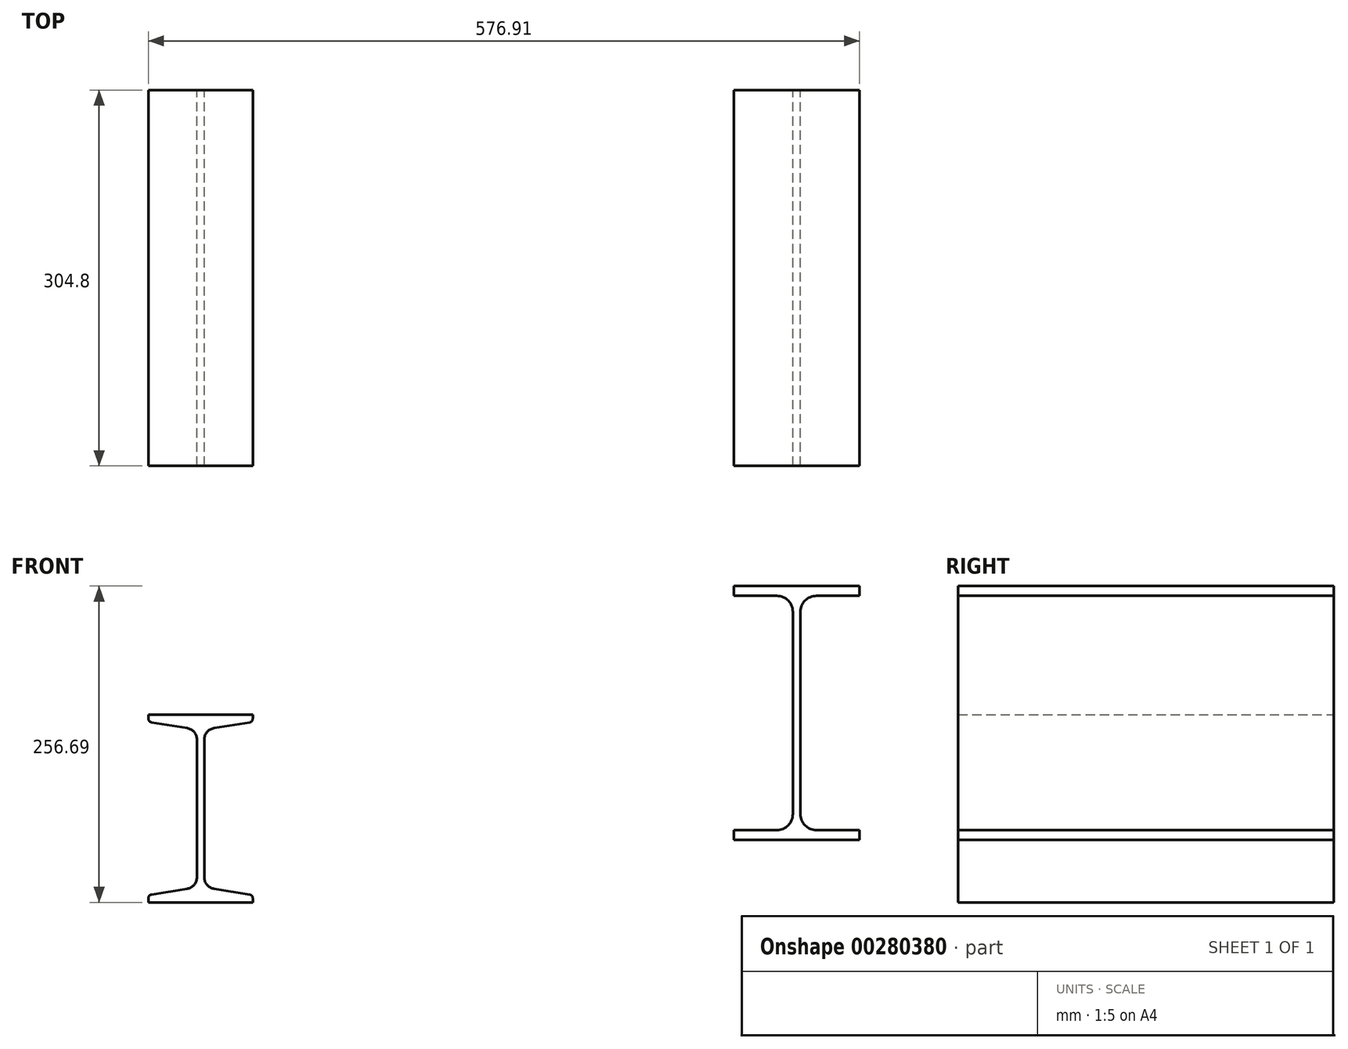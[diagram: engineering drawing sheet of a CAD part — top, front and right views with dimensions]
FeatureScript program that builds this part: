
annotation { "Feature Type Name" : "Feature", "Feature Type Description" : "" }
export const myFeature = defineFeature(function(context is Context, id is Id, definition is map)
    precondition{}
    {
        {
            var Q0;
            Q0=qCreatedBy(makeId("Front.planeOp"),FACE);
            var sketch = newSketch(context, id + "F0", { "sketchPlane" : qUnion([Q0])});
            skLineSegment(sketch, "E0", {"start": v(-460.28, 273.65) * mm, "end": v(-460.28, 271.12) * mm});
            skArc(sketch, "E1", {"start": v(-462.14, 268.95) * mm, "mid": v(-460.8, 269.7) * mm, "end": v(-460.28, 271.12) * mm});
            skLineSegment(sketch, "E2", {"start": v(-460.28, 197.45) * mm, "end": v(-460.28, 199.98) * mm});
            skArc(sketch, "E3", {"start": v(-460.28, 199.98) * mm, "mid": v(-460.8, 201.41) * mm, "end": v(-462.14, 202.16) * mm});
            skArc(sketch, "E4", {"start": v(-483.7, 265.5) * mm, "mid": v(-486.57, 263.88) * mm, "end": v(-487.71, 260.8) * mm});
            skLineSegment(sketch, "E5", {"start": v(-487.71, 210.31) * mm, "end": v(-487.71, 260.8) * mm});
            skLineSegment(sketch, "E6", {"start": v(-492.03, 210.31) * mm, "end": v(-492.03, 260.8) * mm});
            skArc(sketch, "E7", {"start": v(-492.03, 260.8) * mm, "mid": v(-493.17, 263.88) * mm, "end": v(-496.04, 265.5) * mm});
            skArc(sketch, "E8", {"start": v(-496.04, 205.61) * mm, "mid": v(-493.17, 207.22) * mm, "end": v(-492.03, 210.31) * mm});
            skArc(sketch, "E9", {"start": v(-487.71, 210.31) * mm, "mid": v(-486.57, 207.22) * mm, "end": v(-483.7, 205.61) * mm});
            skArc(sketch, "E10", {"start": v(-519.46, 271.12) * mm, "mid": v(-518.94, 269.7) * mm, "end": v(-517.6, 268.95) * mm});
            skLineSegment(sketch, "E11", {"start": v(-519.46, 273.65) * mm, "end": v(-519.46, 271.12) * mm});
            skLineSegment(sketch, "E12", {"start": v(-519.46, 197.45) * mm, "end": v(-519.46, 199.98) * mm});
            skArc(sketch, "E13", {"start": v(-517.6, 202.16) * mm, "mid": v(-518.94, 201.41) * mm, "end": v(-519.46, 199.98) * mm});
            skLineSegment(sketch, "E14", {"start": v(-517.6, 268.95) * mm, "end": v(-496.04, 265.5) * mm});
            skLineSegment(sketch, "E15", {"start": v(-517.6, 202.16) * mm, "end": v(-496.04, 205.61) * mm});
            skLineSegment(sketch, "E16", {"start": v(-462.14, 268.95) * mm, "end": v(-483.7, 265.5) * mm});
            skLineSegment(sketch, "E17", {"start": v(-462.14, 202.16) * mm, "end": v(-483.7, 205.61) * mm});
            skLineSegment(sketch, "E18", {"start": v(-519.46, 273.65) * mm, "end": v(-460.28, 273.65) * mm});
            skLineSegment(sketch, "E19", {"start": v(-519.46, 197.45) * mm, "end": v(-460.28, 197.45) * mm});
            skLineSegment(sketch, "E20", {"start": v(-495.3, 192.02) * mm, "end": v(-484.44, 202.89) * mm});
            skLineSegment(sketch, "E21", {"start": v(-495.3, 202.89) * mm, "end": v(-484.44, 192.02) * mm});
            skLineSegment(sketch, "E22", {"start": v(-351.6, 197.45) * mm, "end": v(-351.6, 222.85) * mm});
            skLineSegment(sketch, "E23", {"start": v(-410.78, 197.45) * mm, "end": v(-410.78, 222.85) * mm});
            skLineSegment(sketch, "E24", {"start": v(-383.35, 197.45) * mm, "end": v(-383.35, 222.85) * mm});
            skLineSegment(sketch, "E25", {"start": v(-379.03, 197.45) * mm, "end": v(-379.03, 222.85) * mm});
            skLineSegment(sketch, "E26", {"start": v(-351.6, 197.45) * mm, "end": v(-410.78, 197.45) * mm});
            skLineSegment(sketch, "E27", {"start": v(-351.6, 222.85) * mm, "end": v(-410.78, 222.85) * mm});
            skLineSegment(sketch, "E28", {"start": v(-386.63, 192.02) * mm, "end": v(-375.76, 202.89) * mm});
            skLineSegment(sketch, "E29", {"start": v(-386.63, 202.89) * mm, "end": v(-375.76, 192.02) * mm});
            skLineSegment(sketch, "E30", {"start": v(-259.79, 273.65) * mm, "end": v(-259.79, 197.45) * mm});
            skLineSegment(sketch, "E31", {"start": v(-285.19, 273.65) * mm, "end": v(-285.19, 197.45) * mm});
            skLineSegment(sketch, "E32", {"start": v(-259.79, 268.95) * mm, "end": v(-285.19, 268.95) * mm});
            skLineSegment(sketch, "E33", {"start": v(-259.79, 273.65) * mm, "end": v(-285.19, 273.65) * mm});
            skLineSegment(sketch, "E34", {"start": v(-259.79, 202.16) * mm, "end": v(-285.19, 202.16) * mm});
            skLineSegment(sketch, "E35", {"start": v(-259.79, 197.45) * mm, "end": v(-285.19, 197.45) * mm});
            skLineSegment(sketch, "E36", {"start": v(-290.62, 192.02) * mm, "end": v(-279.75, 202.89) * mm});
            skLineSegment(sketch, "E37", {"start": v(-290.62, 202.89) * mm, "end": v(-279.75, 192.02) * mm});
            skArc(sketch, "E38", {"start": v(-133.79, 268.95) * mm, "mid": v(-132.46, 269.7) * mm, "end": v(-131.93, 271.12) * mm});
            skLineSegment(sketch, "E39", {"start": v(-131.93, 273.65) * mm, "end": v(-131.93, 271.12) * mm});
            skLineSegment(sketch, "E40", {"start": v(-131.93, 197.45) * mm, "end": v(-131.93, 199.98) * mm});
            skArc(sketch, "E41", {"start": v(-131.93, 199.98) * mm, "mid": v(-132.46, 201.41) * mm, "end": v(-133.79, 202.16) * mm});
            skLineSegment(sketch, "E42", {"start": v(-193.8, 268.95) * mm, "end": v(-172.24, 265.5) * mm});
            skLineSegment(sketch, "E43", {"start": v(-195.66, 273.65) * mm, "end": v(-195.66, 271.12) * mm});
            skArc(sketch, "E44", {"start": v(-195.66, 271.12) * mm, "mid": v(-195.13, 269.7) * mm, "end": v(-193.8, 268.95) * mm});
            skArc(sketch, "E45", {"start": v(-159.36, 210.31) * mm, "mid": v(-158.23, 207.22) * mm, "end": v(-155.35, 205.61) * mm});
            skLineSegment(sketch, "E46", {"start": v(-193.8, 202.16) * mm, "end": v(-172.24, 205.61) * mm});
            skArc(sketch, "E47", {"start": v(-172.24, 205.61) * mm, "mid": v(-169.37, 207.22) * mm, "end": v(-168.23, 210.31) * mm});
            skLineSegment(sketch, "E48", {"start": v(-168.23, 210.31) * mm, "end": v(-168.23, 260.8) * mm});
            skLineSegment(sketch, "E49", {"start": v(-159.36, 210.31) * mm, "end": v(-159.36, 260.8) * mm});
            skLineSegment(sketch, "E50", {"start": v(-195.66, 197.45) * mm, "end": v(-195.66, 199.98) * mm});
            skArc(sketch, "E51", {"start": v(-193.8, 202.16) * mm, "mid": v(-195.13, 201.41) * mm, "end": v(-195.66, 199.98) * mm});
            skArc(sketch, "E52", {"start": v(-168.23, 260.8) * mm, "mid": v(-169.37, 263.88) * mm, "end": v(-172.24, 265.5) * mm});
            skArc(sketch, "E53", {"start": v(-155.35, 265.5) * mm, "mid": v(-158.23, 263.88) * mm, "end": v(-159.36, 260.8) * mm});
            skLineSegment(sketch, "E54", {"start": v(-133.79, 268.95) * mm, "end": v(-155.35, 265.5) * mm});
            skLineSegment(sketch, "E55", {"start": v(-133.79, 202.16) * mm, "end": v(-155.35, 205.61) * mm});
            skLineSegment(sketch, "E56", {"start": v(-195.66, 273.65) * mm, "end": v(-131.93, 273.65) * mm});
            skLineSegment(sketch, "E57", {"start": v(-195.66, 197.45) * mm, "end": v(-131.93, 197.45) * mm});
            skLineSegment(sketch, "E58", {"start": v(-169.23, 192.02) * mm, "end": v(-158.36, 202.89) * mm});
            skLineSegment(sketch, "E59", {"start": v(-169.23, 202.89) * mm, "end": v(-158.36, 192.02) * mm});
            skLineSegment(sketch, "E60", {"start": v(-23.24, 197.45) * mm, "end": v(-23.24, 222.85) * mm});
            skLineSegment(sketch, "E61", {"start": v(-59.54, 197.45) * mm, "end": v(-59.54, 222.85) * mm});
            skLineSegment(sketch, "E62", {"start": v(-50.67, 197.45) * mm, "end": v(-50.67, 222.85) * mm});
            skLineSegment(sketch, "E63", {"start": v(-86.97, 197.45) * mm, "end": v(-86.97, 222.85) * mm});
            skLineSegment(sketch, "E64", {"start": v(-23.24, 222.85) * mm, "end": v(-86.97, 222.85) * mm});
            skLineSegment(sketch, "E65", {"start": v(-23.24, 197.45) * mm, "end": v(-86.97, 197.45) * mm});
            skLineSegment(sketch, "E66", {"start": v(-60.54, 192.02) * mm, "end": v(-49.67, 202.89) * mm});
            skLineSegment(sketch, "E67", {"start": v(-60.54, 202.89) * mm, "end": v(-49.67, 192.02) * mm});
            skLineSegment(sketch, "E68", {"start": v(66.29, 273.65) * mm, "end": v(40.89, 273.65) * mm});
            skLineSegment(sketch, "E69", {"start": v(66.29, 268.95) * mm, "end": v(40.89, 268.95) * mm});
            skLineSegment(sketch, "E70", {"start": v(66.29, 202.16) * mm, "end": v(40.89, 202.16) * mm});
            skLineSegment(sketch, "E71", {"start": v(66.29, 197.45) * mm, "end": v(40.89, 197.45) * mm});
            skLineSegment(sketch, "E72", {"start": v(66.29, 273.65) * mm, "end": v(66.29, 197.45) * mm});
            skLineSegment(sketch, "E73", {"start": v(40.89, 273.65) * mm, "end": v(40.89, 197.45) * mm});
            skLineSegment(sketch, "E74", {"start": v(35.45, 192.02) * mm, "end": v(46.32, 202.89) * mm});
            skLineSegment(sketch, "E75", {"start": v(35.45, 202.89) * mm, "end": v(46.32, 192.02) * mm});
            skLineSegment(sketch, "E76", {"start": v(200.43, 299.05) * mm, "end": v(200.43, 296.42) * mm});
            skArc(sketch, "E77", {"start": v(198.5, 294.16) * mm, "mid": v(199.88, 294.94) * mm, "end": v(200.43, 296.42) * mm});
            skLineSegment(sketch, "E78", {"start": v(200.43, 197.45) * mm, "end": v(200.43, 200.09) * mm});
            skArc(sketch, "E79", {"start": v(200.43, 200.09) * mm, "mid": v(199.88, 201.57) * mm, "end": v(198.5, 202.35) * mm});
            skArc(sketch, "E80", {"start": v(170.08, 289.61) * mm, "mid": v(166.25, 287.46) * mm, "end": v(164.73, 283.34) * mm});
            skArc(sketch, "E81", {"start": v(159.83, 283.34) * mm, "mid": v(158.3, 287.46) * mm, "end": v(154.48, 289.61) * mm});
            skLineSegment(sketch, "E82", {"start": v(126.06, 294.16) * mm, "end": v(154.48, 289.61) * mm});
            skLineSegment(sketch, "E83", {"start": v(124.13, 299.05) * mm, "end": v(124.13, 296.42) * mm});
            skArc(sketch, "E84", {"start": v(124.13, 296.42) * mm, "mid": v(124.68, 294.94) * mm, "end": v(126.06, 294.16) * mm});
            skArc(sketch, "E85", {"start": v(164.73, 213.17) * mm, "mid": v(166.25, 209.05) * mm, "end": v(170.08, 206.9) * mm});
            skArc(sketch, "E86", {"start": v(154.48, 206.9) * mm, "mid": v(158.3, 209.05) * mm, "end": v(159.83, 213.17) * mm});
            skLineSegment(sketch, "E87", {"start": v(126.06, 202.35) * mm, "end": v(154.48, 206.9) * mm});
            skLineSegment(sketch, "E88", {"start": v(124.13, 197.45) * mm, "end": v(124.13, 200.09) * mm});
            skArc(sketch, "E89", {"start": v(126.06, 202.35) * mm, "mid": v(124.68, 201.57) * mm, "end": v(124.13, 200.09) * mm});
            skLineSegment(sketch, "E90", {"start": v(159.83, 213.17) * mm, "end": v(159.83, 283.34) * mm});
            skLineSegment(sketch, "E91", {"start": v(164.73, 213.17) * mm, "end": v(164.73, 283.34) * mm});
            skLineSegment(sketch, "E92", {"start": v(198.5, 294.16) * mm, "end": v(170.08, 289.61) * mm});
            skLineSegment(sketch, "E93", {"start": v(198.5, 202.35) * mm, "end": v(170.08, 206.9) * mm});
            skLineSegment(sketch, "E94", {"start": v(124.13, 299.05) * mm, "end": v(200.43, 299.05) * mm});
            skLineSegment(sketch, "E95", {"start": v(124.13, 197.45) * mm, "end": v(200.43, 197.45) * mm});
            skLineSegment(sketch, "E96", {"start": v(156.84, 192.02) * mm, "end": v(167.71, 202.89) * mm});
            skLineSegment(sketch, "E97", {"start": v(156.84, 202.89) * mm, "end": v(167.71, 192.02) * mm});
            skLineSegment(sketch, "E98", {"start": v(309.12, 197.45) * mm, "end": v(309.12, 222.85) * mm});
            skLineSegment(sketch, "E99", {"start": v(273.42, 197.45) * mm, "end": v(273.42, 222.33) * mm});
            skLineSegment(sketch, "E100", {"start": v(268.52, 197.45) * mm, "end": v(268.52, 222.85) * mm});
            skLineSegment(sketch, "E101", {"start": v(232.82, 197.45) * mm, "end": v(232.82, 222.85) * mm});
            skLineSegment(sketch, "E102", {"start": v(309.12, 222.85) * mm, "end": v(232.82, 222.85) * mm});
            skLineSegment(sketch, "E103", {"start": v(309.12, 197.45) * mm, "end": v(232.82, 197.45) * mm});
            skLineSegment(sketch, "E104", {"start": v(265.54, 192.02) * mm, "end": v(276.4, 202.89) * mm});
            skLineSegment(sketch, "E105", {"start": v(265.54, 202.89) * mm, "end": v(276.4, 192.02) * mm});
            skLineSegment(sketch, "E106", {"start": v(392.36, 299.05) * mm, "end": v(366.96, 299.05) * mm});
            skLineSegment(sketch, "E107", {"start": v(392.36, 294.16) * mm, "end": v(366.96, 294.16) * mm});
            skLineSegment(sketch, "E108", {"start": v(392.36, 202.35) * mm, "end": v(366.96, 202.35) * mm});
            skLineSegment(sketch, "E109", {"start": v(392.36, 197.45) * mm, "end": v(366.96, 197.45) * mm});
            skLineSegment(sketch, "E110", {"start": v(392.36, 299.05) * mm, "end": v(392.36, 197.45) * mm});
            skLineSegment(sketch, "E111", {"start": v(366.96, 299.05) * mm, "end": v(366.96, 197.45) * mm});
            skLineSegment(sketch, "E112", {"start": v(361.53, 192.02) * mm, "end": v(372.4, 202.89) * mm});
            skLineSegment(sketch, "E113", {"start": v(361.53, 202.89) * mm, "end": v(372.4, 192.02) * mm});
            skLineSegment(sketch, "E114", {"start": v(523.86, 299.05) * mm, "end": v(523.86, 296.22) * mm});
            skLineSegment(sketch, "E115", {"start": v(521.79, 293.79) * mm, "end": v(497.84, 289.96) * mm});
            skArc(sketch, "E116", {"start": v(521.79, 293.79) * mm, "mid": v(523.27, 294.62) * mm, "end": v(523.86, 296.22) * mm});
            skLineSegment(sketch, "E117", {"start": v(523.86, 197.45) * mm, "end": v(523.86, 200.28) * mm});
            skLineSegment(sketch, "E118", {"start": v(521.79, 202.72) * mm, "end": v(497.84, 206.55) * mm});
            skArc(sketch, "E119", {"start": v(523.86, 200.28) * mm, "mid": v(523.27, 201.88) * mm, "end": v(521.79, 202.72) * mm});
            skArc(sketch, "E120", {"start": v(484.21, 283.69) * mm, "mid": v(482.7, 287.8) * mm, "end": v(478.87, 289.96) * mm});
            skLineSegment(sketch, "E121", {"start": v(452.84, 299.05) * mm, "end": v(452.84, 296.22) * mm});
            skArc(sketch, "E122", {"start": v(452.84, 296.22) * mm, "mid": v(453.43, 294.62) * mm, "end": v(454.92, 293.79) * mm});
            skLineSegment(sketch, "E123", {"start": v(454.92, 293.79) * mm, "end": v(478.87, 289.96) * mm});
            skArc(sketch, "E124", {"start": v(478.87, 206.55) * mm, "mid": v(482.7, 208.7) * mm, "end": v(484.21, 212.82) * mm});
            skLineSegment(sketch, "E125", {"start": v(452.84, 197.45) * mm, "end": v(452.84, 200.28) * mm});
            skArc(sketch, "E126", {"start": v(454.92, 202.72) * mm, "mid": v(453.43, 201.88) * mm, "end": v(452.84, 200.28) * mm});
            skLineSegment(sketch, "E127", {"start": v(454.92, 202.72) * mm, "end": v(478.87, 206.55) * mm});
            skLineSegment(sketch, "E128", {"start": v(484.21, 212.82) * mm, "end": v(484.21, 283.69) * mm});
            skLineSegment(sketch, "E129", {"start": v(492.5, 212.82) * mm, "end": v(492.5, 283.69) * mm});
            skArc(sketch, "E130", {"start": v(497.84, 289.96) * mm, "mid": v(494.01, 287.8) * mm, "end": v(492.5, 283.69) * mm});
            skArc(sketch, "E131", {"start": v(492.5, 212.82) * mm, "mid": v(494.01, 208.7) * mm, "end": v(497.84, 206.55) * mm});
            skLineSegment(sketch, "E132", {"start": v(452.84, 299.05) * mm, "end": v(523.86, 299.05) * mm});
            skLineSegment(sketch, "E133", {"start": v(452.84, 197.45) * mm, "end": v(523.86, 197.45) * mm});
            skLineSegment(sketch, "E134", {"start": v(482.92, 192.02) * mm, "end": v(493.79, 202.89) * mm});
            skLineSegment(sketch, "E135", {"start": v(482.92, 202.89) * mm, "end": v(493.79, 192.02) * mm});
            skLineSegment(sketch, "E136", {"start": v(-454.36, -34.34) * mm, "end": v(-454.36, -8.94) * mm});
            skLineSegment(sketch, "E137", {"start": v(-494.01, -34.34) * mm, "end": v(-494.01, -8.94) * mm});
            skLineSegment(sketch, "E138", {"start": v(-485.73, -34.34) * mm, "end": v(-485.73, -8.94) * mm});
            skLineSegment(sketch, "E139", {"start": v(-525.38, -34.34) * mm, "end": v(-525.38, -8.94) * mm});
            skLineSegment(sketch, "E140", {"start": v(-454.36, -8.94) * mm, "end": v(-525.38, -8.94) * mm});
            skLineSegment(sketch, "E141", {"start": v(-454.36, -34.34) * mm, "end": v(-525.38, -34.34) * mm});
            skLineSegment(sketch, "E142", {"start": v(-495.3, -39.77) * mm, "end": v(-484.44, -28.9) * mm});
            skLineSegment(sketch, "E143", {"start": v(-495.3, -28.9) * mm, "end": v(-484.44, -39.77) * mm});
            skLineSegment(sketch, "E144", {"start": v(-368.48, 67.26) * mm, "end": v(-368.48, -34.34) * mm});
            skLineSegment(sketch, "E145", {"start": v(-393.88, 67.26) * mm, "end": v(-393.88, -34.34) * mm});
            skLineSegment(sketch, "E146", {"start": v(-368.48, 67.26) * mm, "end": v(-393.88, 67.26) * mm});
            skLineSegment(sketch, "E147", {"start": v(-368.48, 62) * mm, "end": v(-393.88, 62) * mm});
            skLineSegment(sketch, "E148", {"start": v(-368.48, -29.07) * mm, "end": v(-393.88, -29.07) * mm});
            skLineSegment(sketch, "E149", {"start": v(-368.48, -34.34) * mm, "end": v(-393.88, -34.34) * mm});
            skLineSegment(sketch, "E150", {"start": v(-399.31, -39.77) * mm, "end": v(-388.45, -28.9) * mm});
            skLineSegment(sketch, "E151", {"start": v(-399.31, -28.9) * mm, "end": v(-388.45, -39.77) * mm});
            skArc(sketch, "E152", {"start": v(-236.98, 85.96) * mm, "mid": v(-235.09, 87.02) * mm, "end": v(-234.34, 89.06) * mm});
            skLineSegment(sketch, "E153", {"start": v(-234.34, 92.66) * mm, "end": v(-234.34, 89.06) * mm});
            skArc(sketch, "E154", {"start": v(-275.2, 73.94) * mm, "mid": v(-277.1, 79.1) * mm, "end": v(-281.89, 81.78) * mm});
            skArc(sketch, "E155", {"start": v(-263.09, 81.78) * mm, "mid": v(-267.87, 79.1) * mm, "end": v(-269.77, 73.94) * mm});
            skLineSegment(sketch, "E156", {"start": v(-236.98, 85.96) * mm, "end": v(-263.09, 81.78) * mm});
            skArc(sketch, "E157", {"start": v(-234.34, -30.73) * mm, "mid": v(-235.09, -28.7) * mm, "end": v(-236.98, -27.63) * mm});
            skLineSegment(sketch, "E158", {"start": v(-234.34, -34.34) * mm, "end": v(-234.34, -30.73) * mm});
            skArc(sketch, "E159", {"start": v(-269.77, -15.62) * mm, "mid": v(-267.87, -20.77) * mm, "end": v(-263.09, -23.45) * mm});
            skArc(sketch, "E160", {"start": v(-281.89, -23.45) * mm, "mid": v(-277.1, -20.77) * mm, "end": v(-275.2, -15.62) * mm});
            skLineSegment(sketch, "E161", {"start": v(-236.98, -27.63) * mm, "end": v(-263.09, -23.45) * mm});
            skLineSegment(sketch, "E162", {"start": v(-275.2, -15.62) * mm, "end": v(-275.2, 73.94) * mm});
            skLineSegment(sketch, "E163", {"start": v(-269.77, -15.62) * mm, "end": v(-269.77, 73.94) * mm});
            skLineSegment(sketch, "E164", {"start": v(-310.64, 92.66) * mm, "end": v(-310.64, 89.06) * mm});
            skArc(sketch, "E165", {"start": v(-310.64, 89.06) * mm, "mid": v(-309.89, 87.02) * mm, "end": v(-308, 85.96) * mm});
            skArc(sketch, "E166", {"start": v(-308, -27.63) * mm, "mid": v(-309.89, -28.7) * mm, "end": v(-310.64, -30.73) * mm});
            skLineSegment(sketch, "E167", {"start": v(-310.64, -34.34) * mm, "end": v(-310.64, -30.73) * mm});
            skLineSegment(sketch, "E168", {"start": v(-308, 85.96) * mm, "end": v(-281.89, 81.78) * mm});
            skLineSegment(sketch, "E169", {"start": v(-308, -27.63) * mm, "end": v(-281.89, -23.45) * mm});
            skLineSegment(sketch, "E170", {"start": v(-310.64, 92.66) * mm, "end": v(-234.34, 92.66) * mm});
            skLineSegment(sketch, "E171", {"start": v(-310.64, -34.34) * mm, "end": v(-234.34, -34.34) * mm});
            skLineSegment(sketch, "E172", {"start": v(-277.92, -39.77) * mm, "end": v(-267.05, -28.9) * mm});
            skLineSegment(sketch, "E173", {"start": v(-277.92, -28.9) * mm, "end": v(-267.05, -39.77) * mm});
            skLineSegment(sketch, "E174", {"start": v(-125.65, -34.34) * mm, "end": v(-125.65, -8.94) * mm});
            skLineSegment(sketch, "E175", {"start": v(-166.51, -34.34) * mm, "end": v(-166.51, -8.94) * mm});
            skLineSegment(sketch, "E176", {"start": v(-161.08, -34.34) * mm, "end": v(-161.08, -8.94) * mm});
            skLineSegment(sketch, "E177", {"start": v(-201.95, -34.34) * mm, "end": v(-201.95, -8.94) * mm});
            skLineSegment(sketch, "E178", {"start": v(-201.95, -8.94) * mm, "end": v(-125.65, -8.94) * mm});
            skLineSegment(sketch, "E179", {"start": v(-201.95, -34.34) * mm, "end": v(-125.65, -34.34) * mm});
            skLineSegment(sketch, "E180", {"start": v(-169.23, -39.77) * mm, "end": v(-158.36, -28.9) * mm});
            skLineSegment(sketch, "E181", {"start": v(-169.23, -28.9) * mm, "end": v(-158.36, -39.77) * mm});
            skLineSegment(sketch, "E182", {"start": v(-42.4, 92.66) * mm, "end": v(-67.8, 92.66) * mm});
            skLineSegment(sketch, "E183", {"start": v(-42.4, 85.96) * mm, "end": v(-67.8, 85.96) * mm});
            skLineSegment(sketch, "E184", {"start": v(-42.4, -27.63) * mm, "end": v(-67.8, -27.63) * mm});
            skLineSegment(sketch, "E185", {"start": v(-42.4, -34.34) * mm, "end": v(-67.8, -34.34) * mm});
            skLineSegment(sketch, "E186", {"start": v(-42.4, 92.66) * mm, "end": v(-42.4, -34.34) * mm});
            skLineSegment(sketch, "E187", {"start": v(-67.8, 92.66) * mm, "end": v(-67.8, -34.34) * mm});
            skLineSegment(sketch, "E188", {"start": v(-73.24, -39.77) * mm, "end": v(-62.37, -28.9) * mm});
            skLineSegment(sketch, "E189", {"start": v(-73.24, -28.9) * mm, "end": v(-62.37, -39.77) * mm});
            skLineSegment(sketch, "E190", {"start": v(95.3, 92.66) * mm, "end": v(95.3, 89.54) * mm});
            skArc(sketch, "E191", {"start": v(93, 86.85) * mm, "mid": v(94.64, 87.77) * mm, "end": v(95.3, 89.54) * mm});
            skArc(sketch, "E192", {"start": v(66.54, 82.62) * mm, "mid": v(61.76, 79.93) * mm, "end": v(59.86, 74.78) * mm});
            skArc(sketch, "E193", {"start": v(47.31, 74.78) * mm, "mid": v(45.42, 79.93) * mm, "end": v(40.63, 82.62) * mm});
            skLineSegment(sketch, "E194", {"start": v(93, 86.85) * mm, "end": v(66.54, 82.62) * mm});
            skLineSegment(sketch, "E195", {"start": v(95.3, -34.34) * mm, "end": v(95.3, -31.21) * mm});
            skArc(sketch, "E196", {"start": v(95.3, -31.21) * mm, "mid": v(94.64, -29.45) * mm, "end": v(93, -28.52) * mm});
            skArc(sketch, "E197", {"start": v(40.63, -24.3) * mm, "mid": v(45.42, -21.6) * mm, "end": v(47.31, -16.45) * mm});
            skArc(sketch, "E198", {"start": v(59.86, -16.45) * mm, "mid": v(61.76, -21.6) * mm, "end": v(66.54, -24.3) * mm});
            skLineSegment(sketch, "E199", {"start": v(93, -28.52) * mm, "end": v(66.54, -24.3) * mm});
            skLineSegment(sketch, "E200", {"start": v(47.31, -16.45) * mm, "end": v(47.31, 74.78) * mm});
            skLineSegment(sketch, "E201", {"start": v(59.86, -16.45) * mm, "end": v(59.86, 74.78) * mm});
            skLineSegment(sketch, "E202", {"start": v(11.88, 92.66) * mm, "end": v(11.88, 89.54) * mm});
            skArc(sketch, "E203", {"start": v(11.88, 89.54) * mm, "mid": v(12.53, 87.77) * mm, "end": v(14.17, 86.85) * mm});
            skLineSegment(sketch, "E204", {"start": v(11.88, -34.34) * mm, "end": v(11.88, -31.21) * mm});
            skArc(sketch, "E205", {"start": v(14.17, -28.52) * mm, "mid": v(12.53, -29.45) * mm, "end": v(11.88, -31.21) * mm});
            skLineSegment(sketch, "E206", {"start": v(14.17, 86.85) * mm, "end": v(40.63, 82.62) * mm});
            skLineSegment(sketch, "E207", {"start": v(14.17, -28.52) * mm, "end": v(40.63, -24.3) * mm});
            skLineSegment(sketch, "E208", {"start": v(11.88, 92.66) * mm, "end": v(95.3, 92.66) * mm});
            skLineSegment(sketch, "E209", {"start": v(11.88, -34.34) * mm, "end": v(95.3, -34.34) * mm});
            skLineSegment(sketch, "E210", {"start": v(48.15, -39.77) * mm, "end": v(59.02, -28.9) * mm});
            skLineSegment(sketch, "E211", {"start": v(48.15, -28.9) * mm, "end": v(59.02, -39.77) * mm});
            skLineSegment(sketch, "E212", {"start": v(203.99, -34.34) * mm, "end": v(203.99, -8.94) * mm});
            skLineSegment(sketch, "E213", {"start": v(156, -34.34) * mm, "end": v(156, -8.94) * mm});
            skLineSegment(sketch, "E214", {"start": v(168.55, -34.34) * mm, "end": v(168.55, -8.94) * mm});
            skLineSegment(sketch, "E215", {"start": v(120.57, -34.34) * mm, "end": v(120.57, -8.94) * mm});
            skLineSegment(sketch, "E216", {"start": v(203.99, -8.94) * mm, "end": v(120.57, -8.94) * mm});
            skLineSegment(sketch, "E217", {"start": v(203.99, -34.34) * mm, "end": v(120.57, -34.34) * mm});
            skLineSegment(sketch, "E218", {"start": v(156.84, -39.77) * mm, "end": v(167.71, -28.9) * mm});
            skLineSegment(sketch, "E219", {"start": v(156.84, -28.9) * mm, "end": v(167.71, -39.77) * mm});
            skLineSegment(sketch, "E220", {"start": v(283.67, 92.66) * mm, "end": v(258.27, 92.66) * mm});
            skLineSegment(sketch, "E221", {"start": v(283.67, 86.85) * mm, "end": v(258.27, 86.85) * mm});
            skLineSegment(sketch, "E222", {"start": v(283.67, -28.52) * mm, "end": v(258.27, -28.52) * mm});
            skLineSegment(sketch, "E223", {"start": v(283.67, -34.34) * mm, "end": v(258.27, -34.34) * mm});
            skLineSegment(sketch, "E224", {"start": v(283.67, 92.66) * mm, "end": v(283.67, -34.34) * mm});
            skLineSegment(sketch, "E225", {"start": v(258.27, 92.66) * mm, "end": v(258.27, -34.34) * mm});
            skLineSegment(sketch, "E226", {"start": v(252.84, -39.77) * mm, "end": v(263.7, -28.9) * mm});
            skLineSegment(sketch, "E227", {"start": v(252.84, -28.9) * mm, "end": v(263.7, -39.77) * mm});
            skArc(sketch, "E228", {"start": v(419.47, 111.7) * mm, "mid": v(421.26, 112.7) * mm, "end": v(421.98, 114.64) * mm});
            skArc(sketch, "E229", {"start": v(390.63, 107.08) * mm, "mid": v(384.89, 103.85) * mm, "end": v(382.6, 97.67) * mm});
            skArc(sketch, "E230", {"start": v(376.72, 97.67) * mm, "mid": v(374.44, 103.85) * mm, "end": v(368.7, 107.08) * mm});
            skLineSegment(sketch, "E231", {"start": v(419.47, 111.7) * mm, "end": v(390.63, 107.08) * mm});
            skLineSegment(sketch, "E232", {"start": v(421.98, 118.06) * mm, "end": v(421.98, 114.64) * mm});
            skLineSegment(sketch, "E233", {"start": v(421.98, -34.34) * mm, "end": v(421.98, -30.91) * mm});
            skArc(sketch, "E234", {"start": v(421.98, -30.91) * mm, "mid": v(421.26, -28.98) * mm, "end": v(419.47, -27.97) * mm});
            skArc(sketch, "E235", {"start": v(382.6, -13.95) * mm, "mid": v(384.89, -20.13) * mm, "end": v(390.63, -23.35) * mm});
            skArc(sketch, "E236", {"start": v(368.7, -23.35) * mm, "mid": v(374.44, -20.13) * mm, "end": v(376.72, -13.95) * mm});
            skLineSegment(sketch, "E237", {"start": v(419.47, -27.97) * mm, "end": v(390.63, -23.35) * mm});
            skLineSegment(sketch, "E238", {"start": v(376.72, -13.95) * mm, "end": v(376.72, 97.67) * mm});
            skLineSegment(sketch, "E239", {"start": v(382.6, -13.95) * mm, "end": v(382.6, 97.67) * mm});
            skArc(sketch, "E240", {"start": v(337.35, 114.64) * mm, "mid": v(338.06, 112.7) * mm, "end": v(339.86, 111.7) * mm});
            skLineSegment(sketch, "E241", {"start": v(337.35, 118.06) * mm, "end": v(337.35, 114.64) * mm});
            skLineSegment(sketch, "E242", {"start": v(337.35, -34.34) * mm, "end": v(337.35, -30.91) * mm});
            skArc(sketch, "E243", {"start": v(339.86, -27.97) * mm, "mid": v(338.06, -28.98) * mm, "end": v(337.35, -30.91) * mm});
            skLineSegment(sketch, "E244", {"start": v(339.86, 111.7) * mm, "end": v(368.7, 107.08) * mm});
            skLineSegment(sketch, "E245", {"start": v(339.86, -27.97) * mm, "end": v(368.7, -23.35) * mm});
            skLineSegment(sketch, "E246", {"start": v(337.35, 118.06) * mm, "end": v(421.98, 118.06) * mm});
            skLineSegment(sketch, "E247", {"start": v(337.35, -34.34) * mm, "end": v(421.98, -34.34) * mm});
            skLineSegment(sketch, "E248", {"start": v(374.23, -39.77) * mm, "end": v(385.1, -28.9) * mm});
            skLineSegment(sketch, "E249", {"start": v(374.23, -28.9) * mm, "end": v(385.1, -39.77) * mm});
            skLineSegment(sketch, "E250", {"start": v(530.66, -34.34) * mm, "end": v(530.66, -8.94) * mm});
            skLineSegment(sketch, "E251", {"start": v(491.29, -34.34) * mm, "end": v(491.29, -8.94) * mm});
            skLineSegment(sketch, "E252", {"start": v(485.4, -34.34) * mm, "end": v(485.4, -8.94) * mm});
            skLineSegment(sketch, "E253", {"start": v(446.02, -34.34) * mm, "end": v(446.02, -8.94) * mm});
            skLineSegment(sketch, "E254", {"start": v(530.66, -8.94) * mm, "end": v(446.02, -8.94) * mm});
            skLineSegment(sketch, "E255", {"start": v(530.66, -34.34) * mm, "end": v(446.02, -34.34) * mm});
            skLineSegment(sketch, "E256", {"start": v(482.9, -39.77) * mm, "end": v(493.78, -28.9) * mm});
            skLineSegment(sketch, "E257", {"start": v(482.9, -28.9) * mm, "end": v(493.78, -39.77) * mm});
            skLineSegment(sketch, "E258", {"start": v(-477.17, -113.73) * mm, "end": v(-502.57, -113.73) * mm});
            skLineSegment(sketch, "E259", {"start": v(-477.17, -120.1) * mm, "end": v(-502.57, -120.1) * mm});
            skLineSegment(sketch, "E260", {"start": v(-477.17, -259.76) * mm, "end": v(-502.57, -259.76) * mm});
            skLineSegment(sketch, "E261", {"start": v(-477.17, -266.13) * mm, "end": v(-502.57, -266.13) * mm});
            skLineSegment(sketch, "E262", {"start": v(-477.17, -113.73) * mm, "end": v(-477.17, -266.13) * mm});
            skLineSegment(sketch, "E263", {"start": v(-502.57, -113.73) * mm, "end": v(-502.57, -266.13) * mm});
            skLineSegment(sketch, "E264", {"start": v(-508, -271.56) * mm, "end": v(-497.14, -260.7) * mm});
            skLineSegment(sketch, "E265", {"start": v(-508, -260.7) * mm, "end": v(-497.14, -271.56) * mm});
            skLineSegment(sketch, "E266", {"start": v(-335.9, -113.73) * mm, "end": v(-335.9, -117.15) * mm});
            skArc(sketch, "E267", {"start": v(-338.42, -120.1) * mm, "mid": v(-336.62, -119.09) * mm, "end": v(-335.9, -117.15) * mm});
            skArc(sketch, "E268", {"start": v(-367.25, -124.71) * mm, "mid": v(-373, -127.94) * mm, "end": v(-375.27, -134.12) * mm});
            skLineSegment(sketch, "E269", {"start": v(-338.42, -120.1) * mm, "end": v(-367.25, -124.71) * mm});
            skLineSegment(sketch, "E270", {"start": v(-375.27, -245.74) * mm, "end": v(-375.27, -134.12) * mm});
            skLineSegment(sketch, "E271", {"start": v(-426.46, -113.73) * mm, "end": v(-426.46, -117.15) * mm});
            skArc(sketch, "E272", {"start": v(-387.09, -134.12) * mm, "mid": v(-389.36, -127.94) * mm, "end": v(-395.1, -124.71) * mm});
            skLineSegment(sketch, "E273", {"start": v(-423.94, -120.1) * mm, "end": v(-395.1, -124.71) * mm});
            skArc(sketch, "E274", {"start": v(-426.46, -117.15) * mm, "mid": v(-425.74, -119.09) * mm, "end": v(-423.94, -120.1) * mm});
            skLineSegment(sketch, "E275", {"start": v(-387.09, -245.74) * mm, "end": v(-387.09, -134.12) * mm});
            skLineSegment(sketch, "E276", {"start": v(-426.46, -113.73) * mm, "end": v(-335.9, -113.73) * mm});
            skLineSegment(sketch, "E277", {"start": v(-335.9, -266.13) * mm, "end": v(-335.9, -262.7) * mm});
            skArc(sketch, "E278", {"start": v(-335.9, -262.7) * mm, "mid": v(-336.62, -260.77) * mm, "end": v(-338.42, -259.76) * mm});
            skLineSegment(sketch, "E279", {"start": v(-338.42, -259.76) * mm, "end": v(-367.25, -255.14) * mm});
            skLineSegment(sketch, "E280", {"start": v(-426.46, -266.13) * mm, "end": v(-426.46, -262.7) * mm});
            skLineSegment(sketch, "E281", {"start": v(-423.94, -259.76) * mm, "end": v(-395.1, -255.14) * mm});
            skArc(sketch, "E282", {"start": v(-423.94, -259.76) * mm, "mid": v(-425.74, -260.77) * mm, "end": v(-426.46, -262.7) * mm});
            skLineSegment(sketch, "E283", {"start": v(-426.46, -266.13) * mm, "end": v(-335.9, -266.13) * mm});
            skArc(sketch, "E284", {"start": v(-395.1, -255.14) * mm, "mid": v(-389.36, -251.92) * mm, "end": v(-387.09, -245.74) * mm});
            skArc(sketch, "E285", {"start": v(-375.27, -245.74) * mm, "mid": v(-373, -251.92) * mm, "end": v(-367.25, -255.14) * mm});
            skLineSegment(sketch, "E286", {"start": v(-386.61, -271.56) * mm, "end": v(-375.75, -260.7) * mm});
            skLineSegment(sketch, "E287", {"start": v(-386.61, -260.7) * mm, "end": v(-375.75, -271.56) * mm});
            skLineSegment(sketch, "E288", {"start": v(-227.21, -240.73) * mm, "end": v(-317.76, -240.73) * mm});
            skLineSegment(sketch, "E289", {"start": v(-227.21, -266.13) * mm, "end": v(-317.76, -266.13) * mm});
            skLineSegment(sketch, "E290", {"start": v(-227.21, -266.13) * mm, "end": v(-227.21, -240.73) * mm});
            skLineSegment(sketch, "E291", {"start": v(-317.76, -266.13) * mm, "end": v(-317.76, -240.73) * mm});
            skLineSegment(sketch, "E292", {"start": v(-278.4, -266.13) * mm, "end": v(-278.4, -240.73) * mm});
            skLineSegment(sketch, "E293", {"start": v(-266.58, -266.13) * mm, "end": v(-266.58, -240.73) * mm});
            skLineSegment(sketch, "E294", {"start": v(-277.92, -271.56) * mm, "end": v(-267.05, -260.7) * mm});
            skLineSegment(sketch, "E295", {"start": v(-277.92, -260.7) * mm, "end": v(-267.05, -271.56) * mm});
            skLineSegment(sketch, "E296", {"start": v(-151.1, -113.73) * mm, "end": v(-176.5, -113.73) * mm});
            skLineSegment(sketch, "E297", {"start": v(-151.1, -120.1) * mm, "end": v(-176.5, -120.1) * mm});
            skLineSegment(sketch, "E298", {"start": v(-151.1, -259.76) * mm, "end": v(-176.5, -259.76) * mm});
            skLineSegment(sketch, "E299", {"start": v(-151.1, -266.13) * mm, "end": v(-176.5, -266.13) * mm});
            skLineSegment(sketch, "E300", {"start": v(-151.1, -113.73) * mm, "end": v(-151.1, -266.13) * mm});
            skLineSegment(sketch, "E301", {"start": v(-176.5, -113.73) * mm, "end": v(-176.5, -266.13) * mm});
            skLineSegment(sketch, "E302", {"start": v(-181.93, -271.56) * mm, "end": v(-171.06, -260.7) * mm});
            skLineSegment(sketch, "E303", {"start": v(-181.93, -260.7) * mm, "end": v(-171.06, -271.56) * mm});
            skSolve(sketch);
        }
        {
            var Q0;
            Q0 = qSketchRegion(id + "F0", true);
            extrude(context, id + "F1", {"entities" : qUnion([Q0]), "depth" : 304.8 * mm});
        }
        {
            var Q0;
            Q0=makeQuery(id+"F1.opExtrude","SWEPT_BODY",BODY,{"disambiguationData":[OSD([sQuery(id+"F0.wireOp",EDGE,"E144"),sQuery(id+"F0.wireOp",EDGE,"E145"),sQuery(id+"F0.wireOp",EDGE,"E146"),sQuery(id+"F0.wireOp",EDGE,"E149")])]});
            var Q1;
            Q1=makeQuery(id+"F1.opExtrude","SWEPT_BODY",BODY,{"disambiguationData":[OSD([sQuery(id+"F0.wireOp",EDGE,"E0"),sQuery(id+"F0.wireOp",EDGE,"E1"),sQuery(id+"F0.wireOp",EDGE,"E2"),sQuery(id+"F0.wireOp",EDGE,"E3"),sQuery(id+"F0.wireOp",EDGE,"E4"),sQuery(id+"F0.wireOp",EDGE,"E5"),sQuery(id+"F0.wireOp",EDGE,"E6"),sQuery(id+"F0.wireOp",EDGE,"E7"),sQuery(id+"F0.wireOp",EDGE,"E8"),sQuery(id+"F0.wireOp",EDGE,"E9"),sQuery(id+"F0.wireOp",EDGE,"E10"),sQuery(id+"F0.wireOp",EDGE,"E11"),sQuery(id+"F0.wireOp",EDGE,"E12"),sQuery(id+"F0.wireOp",EDGE,"E13"),sQuery(id+"F0.wireOp",EDGE,"E14"),sQuery(id+"F0.wireOp",EDGE,"E15"),sQuery(id+"F0.wireOp",EDGE,"E16"),sQuery(id+"F0.wireOp",EDGE,"E17"),sQuery(id+"F0.wireOp",EDGE,"E18"),sQuery(id+"F0.wireOp",EDGE,"E19")])]});
            var Q2;
            Q2=makeQuery(id+"F1.opExtrude","SWEPT_BODY",BODY,{"disambiguationData":[OSD([sQuery(id+"F0.wireOp",EDGE,"E22"),sQuery(id+"F0.wireOp",EDGE,"E23"),sQuery(id+"F0.wireOp",EDGE,"E26"),sQuery(id+"F0.wireOp",EDGE,"E27")])]});
            var Q3;
            Q3=makeQuery(id+"F1.opExtrude","SWEPT_BODY",BODY,{"disambiguationData":[OSD([sQuery(id+"F0.wireOp",EDGE,"E30"),sQuery(id+"F0.wireOp",EDGE,"E31"),sQuery(id+"F0.wireOp",EDGE,"E33"),sQuery(id+"F0.wireOp",EDGE,"E35")])]});
            var Q4;
            Q4=makeQuery(id+"F1.opExtrude","SWEPT_BODY",BODY,{"disambiguationData":[OSD([sQuery(id+"F0.wireOp",EDGE,"E38"),sQuery(id+"F0.wireOp",EDGE,"E39"),sQuery(id+"F0.wireOp",EDGE,"E40"),sQuery(id+"F0.wireOp",EDGE,"E41"),sQuery(id+"F0.wireOp",EDGE,"E42"),sQuery(id+"F0.wireOp",EDGE,"E43"),sQuery(id+"F0.wireOp",EDGE,"E44"),sQuery(id+"F0.wireOp",EDGE,"E45"),sQuery(id+"F0.wireOp",EDGE,"E46"),sQuery(id+"F0.wireOp",EDGE,"E47"),sQuery(id+"F0.wireOp",EDGE,"E48"),sQuery(id+"F0.wireOp",EDGE,"E49"),sQuery(id+"F0.wireOp",EDGE,"E50"),sQuery(id+"F0.wireOp",EDGE,"E51"),sQuery(id+"F0.wireOp",EDGE,"E52"),sQuery(id+"F0.wireOp",EDGE,"E53"),sQuery(id+"F0.wireOp",EDGE,"E54"),sQuery(id+"F0.wireOp",EDGE,"E55"),sQuery(id+"F0.wireOp",EDGE,"E56"),sQuery(id+"F0.wireOp",EDGE,"E57")])]});
            var Q5;
            Q5=makeQuery(id+"F1.opExtrude","SWEPT_BODY",BODY,{"disambiguationData":[OSD([sQuery(id+"F0.wireOp",EDGE,"E60"),sQuery(id+"F0.wireOp",EDGE,"E63"),sQuery(id+"F0.wireOp",EDGE,"E64"),sQuery(id+"F0.wireOp",EDGE,"E65")])]});
            var Q6;
            Q6=makeQuery(id+"F1.opExtrude","SWEPT_BODY",BODY,{"disambiguationData":[OSD([sQuery(id+"F0.wireOp",EDGE,"E68"),sQuery(id+"F0.wireOp",EDGE,"E71"),sQuery(id+"F0.wireOp",EDGE,"E72"),sQuery(id+"F0.wireOp",EDGE,"E73")])]});
            var Q7;
            Q7=makeQuery(id+"F1.opExtrude","SWEPT_BODY",BODY,{"disambiguationData":[OSD([sQuery(id+"F0.wireOp",EDGE,"E76"),sQuery(id+"F0.wireOp",EDGE,"E77"),sQuery(id+"F0.wireOp",EDGE,"E78"),sQuery(id+"F0.wireOp",EDGE,"E79"),sQuery(id+"F0.wireOp",EDGE,"E80"),sQuery(id+"F0.wireOp",EDGE,"E81"),sQuery(id+"F0.wireOp",EDGE,"E82"),sQuery(id+"F0.wireOp",EDGE,"E83"),sQuery(id+"F0.wireOp",EDGE,"E84"),sQuery(id+"F0.wireOp",EDGE,"E85"),sQuery(id+"F0.wireOp",EDGE,"E86"),sQuery(id+"F0.wireOp",EDGE,"E87"),sQuery(id+"F0.wireOp",EDGE,"E88"),sQuery(id+"F0.wireOp",EDGE,"E89"),sQuery(id+"F0.wireOp",EDGE,"E90"),sQuery(id+"F0.wireOp",EDGE,"E91"),sQuery(id+"F0.wireOp",EDGE,"E92"),sQuery(id+"F0.wireOp",EDGE,"E93"),sQuery(id+"F0.wireOp",EDGE,"E94"),sQuery(id+"F0.wireOp",EDGE,"E95")])]});
            var Q8;
            Q8=makeQuery(id+"F1.opExtrude","SWEPT_BODY",BODY,{"disambiguationData":[OSD([sQuery(id+"F0.wireOp",EDGE,"E98"),sQuery(id+"F0.wireOp",EDGE,"E101"),sQuery(id+"F0.wireOp",EDGE,"E102"),sQuery(id+"F0.wireOp",EDGE,"E103")])]});
            var Q9;
            Q9=makeQuery(id+"F1.opExtrude","SWEPT_BODY",BODY,{"disambiguationData":[OSD([sQuery(id+"F0.wireOp",EDGE,"E106"),sQuery(id+"F0.wireOp",EDGE,"E109"),sQuery(id+"F0.wireOp",EDGE,"E110"),sQuery(id+"F0.wireOp",EDGE,"E111")])]});
            var Q10;
            Q10=makeQuery(id+"F1.opExtrude","SWEPT_BODY",BODY,{"disambiguationData":[OSD([sQuery(id+"F0.wireOp",EDGE,"E114"),sQuery(id+"F0.wireOp",EDGE,"E115"),sQuery(id+"F0.wireOp",EDGE,"E116"),sQuery(id+"F0.wireOp",EDGE,"E117"),sQuery(id+"F0.wireOp",EDGE,"E118"),sQuery(id+"F0.wireOp",EDGE,"E119"),sQuery(id+"F0.wireOp",EDGE,"E120"),sQuery(id+"F0.wireOp",EDGE,"E121"),sQuery(id+"F0.wireOp",EDGE,"E122"),sQuery(id+"F0.wireOp",EDGE,"E123"),sQuery(id+"F0.wireOp",EDGE,"E124"),sQuery(id+"F0.wireOp",EDGE,"E125"),sQuery(id+"F0.wireOp",EDGE,"E126"),sQuery(id+"F0.wireOp",EDGE,"E127"),sQuery(id+"F0.wireOp",EDGE,"E128"),sQuery(id+"F0.wireOp",EDGE,"E129"),sQuery(id+"F0.wireOp",EDGE,"E130"),sQuery(id+"F0.wireOp",EDGE,"E131"),sQuery(id+"F0.wireOp",EDGE,"E132"),sQuery(id+"F0.wireOp",EDGE,"E133")])]});
            var Q11;
            Q11=makeQuery(id+"F1.opExtrude","SWEPT_BODY",BODY,{"disambiguationData":[OSD([sQuery(id+"F0.wireOp",EDGE,"E136"),sQuery(id+"F0.wireOp",EDGE,"E139"),sQuery(id+"F0.wireOp",EDGE,"E140"),sQuery(id+"F0.wireOp",EDGE,"E141")])]});
            var Q12;
            Q12=makeQuery(id+"F1.opExtrude","SWEPT_BODY",BODY,{"disambiguationData":[OSD([sQuery(id+"F0.wireOp",EDGE,"E174"),sQuery(id+"F0.wireOp",EDGE,"E177"),sQuery(id+"F0.wireOp",EDGE,"E178"),sQuery(id+"F0.wireOp",EDGE,"E179")])]});
            var Q13;
            Q13=makeQuery(id+"F1.opExtrude","SWEPT_BODY",BODY,{"disambiguationData":[OSD([sQuery(id+"F0.wireOp",EDGE,"E182"),sQuery(id+"F0.wireOp",EDGE,"E185"),sQuery(id+"F0.wireOp",EDGE,"E186"),sQuery(id+"F0.wireOp",EDGE,"E187")])]});
            var Q14;
            Q14=makeQuery(id+"F1.opExtrude","SWEPT_BODY",BODY,{"disambiguationData":[OSD([sQuery(id+"F0.wireOp",EDGE,"E190"),sQuery(id+"F0.wireOp",EDGE,"E191"),sQuery(id+"F0.wireOp",EDGE,"E192"),sQuery(id+"F0.wireOp",EDGE,"E193"),sQuery(id+"F0.wireOp",EDGE,"E194"),sQuery(id+"F0.wireOp",EDGE,"E195"),sQuery(id+"F0.wireOp",EDGE,"E196"),sQuery(id+"F0.wireOp",EDGE,"E197"),sQuery(id+"F0.wireOp",EDGE,"E198"),sQuery(id+"F0.wireOp",EDGE,"E199"),sQuery(id+"F0.wireOp",EDGE,"E200"),sQuery(id+"F0.wireOp",EDGE,"E201"),sQuery(id+"F0.wireOp",EDGE,"E202"),sQuery(id+"F0.wireOp",EDGE,"E203"),sQuery(id+"F0.wireOp",EDGE,"E204"),sQuery(id+"F0.wireOp",EDGE,"E205"),sQuery(id+"F0.wireOp",EDGE,"E206"),sQuery(id+"F0.wireOp",EDGE,"E207"),sQuery(id+"F0.wireOp",EDGE,"E208"),sQuery(id+"F0.wireOp",EDGE,"E209")])]});
            var Q15;
            Q15=makeQuery(id+"F1.opExtrude","SWEPT_BODY",BODY,{"disambiguationData":[OSD([sQuery(id+"F0.wireOp",EDGE,"E212"),sQuery(id+"F0.wireOp",EDGE,"E215"),sQuery(id+"F0.wireOp",EDGE,"E216"),sQuery(id+"F0.wireOp",EDGE,"E217")])]});
            var Q16;
            Q16=makeQuery(id+"F1.opExtrude","SWEPT_BODY",BODY,{"disambiguationData":[OSD([sQuery(id+"F0.wireOp",EDGE,"E220"),sQuery(id+"F0.wireOp",EDGE,"E223"),sQuery(id+"F0.wireOp",EDGE,"E224"),sQuery(id+"F0.wireOp",EDGE,"E225")])]});
            var Q17;
            Q17=makeQuery(id+"F1.opExtrude","SWEPT_BODY",BODY,{"disambiguationData":[OSD([sQuery(id+"F0.wireOp",EDGE,"E250"),sQuery(id+"F0.wireOp",EDGE,"E253"),sQuery(id+"F0.wireOp",EDGE,"E254"),sQuery(id+"F0.wireOp",EDGE,"E255")])]});
            var Q18;
            Q18=makeQuery(id+"F1.opExtrude","SWEPT_BODY",BODY,{"disambiguationData":[OSD([sQuery(id+"F0.wireOp",EDGE,"E258"),sQuery(id+"F0.wireOp",EDGE,"E261"),sQuery(id+"F0.wireOp",EDGE,"E262"),sQuery(id+"F0.wireOp",EDGE,"E263")])]});
            var Q19;
            Q19=makeQuery(id+"F1.opExtrude","SWEPT_BODY",BODY,{"disambiguationData":[OSD([sQuery(id+"F0.wireOp",EDGE,"E266"),sQuery(id+"F0.wireOp",EDGE,"E267"),sQuery(id+"F0.wireOp",EDGE,"E268"),sQuery(id+"F0.wireOp",EDGE,"E269"),sQuery(id+"F0.wireOp",EDGE,"E270"),sQuery(id+"F0.wireOp",EDGE,"E271"),sQuery(id+"F0.wireOp",EDGE,"E272"),sQuery(id+"F0.wireOp",EDGE,"E273"),sQuery(id+"F0.wireOp",EDGE,"E274"),sQuery(id+"F0.wireOp",EDGE,"E275"),sQuery(id+"F0.wireOp",EDGE,"E276"),sQuery(id+"F0.wireOp",EDGE,"E277"),sQuery(id+"F0.wireOp",EDGE,"E278"),sQuery(id+"F0.wireOp",EDGE,"E279"),sQuery(id+"F0.wireOp",EDGE,"E280"),sQuery(id+"F0.wireOp",EDGE,"E281"),sQuery(id+"F0.wireOp",EDGE,"E282"),sQuery(id+"F0.wireOp",EDGE,"E283"),sQuery(id+"F0.wireOp",EDGE,"E284"),sQuery(id+"F0.wireOp",EDGE,"E285")])]});
            var Q20;
            Q20=makeQuery(id+"F1.opExtrude","SWEPT_BODY",BODY,{"disambiguationData":[OSD([sQuery(id+"F0.wireOp",EDGE,"E288"),sQuery(id+"F0.wireOp",EDGE,"E289"),sQuery(id+"F0.wireOp",EDGE,"E290"),sQuery(id+"F0.wireOp",EDGE,"E291")])]});
            var Q21;
            Q21=makeQuery(id+"F1.opExtrude","SWEPT_BODY",BODY,{"disambiguationData":[OSD([sQuery(id+"F0.wireOp",EDGE,"E296"),sQuery(id+"F0.wireOp",EDGE,"E299"),sQuery(id+"F0.wireOp",EDGE,"E300"),sQuery(id+"F0.wireOp",EDGE,"E301")])]});
            var Q22;
            Q22=makeQuery(id+"F1.opExtrude","SWEPT_BODY",BODY,{"disambiguationData":[OSD([sQuery(id+"F0.wireOp",EDGE,"E152"),sQuery(id+"F0.wireOp",EDGE,"E153"),sQuery(id+"F0.wireOp",EDGE,"E154"),sQuery(id+"F0.wireOp",EDGE,"E155"),sQuery(id+"F0.wireOp",EDGE,"E156"),sQuery(id+"F0.wireOp",EDGE,"E157"),sQuery(id+"F0.wireOp",EDGE,"E158"),sQuery(id+"F0.wireOp",EDGE,"E159"),sQuery(id+"F0.wireOp",EDGE,"E160"),sQuery(id+"F0.wireOp",EDGE,"E161"),sQuery(id+"F0.wireOp",EDGE,"E162"),sQuery(id+"F0.wireOp",EDGE,"E163"),sQuery(id+"F0.wireOp",EDGE,"E164"),sQuery(id+"F0.wireOp",EDGE,"E165"),sQuery(id+"F0.wireOp",EDGE,"E166"),sQuery(id+"F0.wireOp",EDGE,"E167"),sQuery(id+"F0.wireOp",EDGE,"E168"),sQuery(id+"F0.wireOp",EDGE,"E169"),sQuery(id+"F0.wireOp",EDGE,"E170"),sQuery(id+"F0.wireOp",EDGE,"E171")])]});
            deleteBodies(context, id + "F2", {"entities" : qUnion([Q0, Q1, Q2, Q3, Q4, Q5, Q6, Q7, Q8, Q9, Q10, Q11, Q12, Q13, Q14, Q15, Q16, Q17, Q18, Q19, Q20, Q21, Q22])});
        }
        {
            var Q0;
            Q0=qCreatedBy(makeId("Front.planeOp"),FACE);
            var sketch = newSketch(context, id + "F3", { "sketchPlane" : qUnion([Q0])});
            skLineSegment(sketch, "E304", {"start": v(-1413.58, 757.04) * mm, "end": v(-1310.45, 757.04) * mm});
            skLineSegment(sketch, "E305", {"start": v(-1413.58, 862.7) * mm, "end": v(-1310.45, 862.7) * mm});
            skLineSegment(sketch, "E306", {"start": v(-1351.86, 765.8) * mm, "end": v(-1310.45, 765.8) * mm});
            skLineSegment(sketch, "E307", {"start": v(-1351.86, 853.94) * mm, "end": v(-1310.45, 853.94) * mm});
            skLineSegment(sketch, "E308", {"start": v(-1365.57, 772.41) * mm, "end": v(-1365.57, 847.34) * mm});
            skLineSegment(sketch, "E309", {"start": v(-1358.46, 772.41) * mm, "end": v(-1358.46, 847.34) * mm});
            skLineSegment(sketch, "E310", {"start": v(-1413.58, 765.8) * mm, "end": v(-1372.18, 765.8) * mm});
            skLineSegment(sketch, "E311", {"start": v(-1413.58, 757.04) * mm, "end": v(-1413.58, 765.8) * mm});
            skArc(sketch, "E312", {"start": v(-1372.18, 765.8) * mm, "mid": v(-1367.5, 767.74) * mm, "end": v(-1365.57, 772.41) * mm});
            skArc(sketch, "E313", {"start": v(-1358.46, 772.41) * mm, "mid": v(-1356.52, 767.74) * mm, "end": v(-1351.86, 765.8) * mm});
            skLineSegment(sketch, "E314", {"start": v(-1413.58, 862.7) * mm, "end": v(-1413.58, 853.94) * mm});
            skLineSegment(sketch, "E315", {"start": v(-1413.58, 853.94) * mm, "end": v(-1372.18, 853.94) * mm});
            skArc(sketch, "E316", {"start": v(-1365.57, 847.34) * mm, "mid": v(-1367.5, 852.01) * mm, "end": v(-1372.18, 853.94) * mm});
            skArc(sketch, "E317", {"start": v(-1351.86, 853.94) * mm, "mid": v(-1356.52, 852.01) * mm, "end": v(-1358.46, 847.34) * mm});
            skLineSegment(sketch, "E318", {"start": v(-1310.45, 757.04) * mm, "end": v(-1310.45, 765.8) * mm});
            skLineSegment(sketch, "E319", {"start": v(-1310.45, 862.7) * mm, "end": v(-1310.45, 853.94) * mm});
            skLineSegment(sketch, "E320", {"start": v(-1374.38, 744.68) * mm, "end": v(-1349.65, 769.4) * mm});
            skLineSegment(sketch, "E321", {"start": v(-1374.38, 769.4) * mm, "end": v(-1349.65, 744.68) * mm});
            skLineSegment(sketch, "E322", {"start": v(-1063.21, 757.04) * mm, "end": v(-1063.21, 782.44) * mm});
            skLineSegment(sketch, "E323", {"start": v(-1166.34, 782.44) * mm, "end": v(-1166.34, 757.04) * mm});
            skLineSegment(sketch, "E324", {"start": v(-1118.33, 757.04) * mm, "end": v(-1118.33, 782.44) * mm});
            skLineSegment(sketch, "E325", {"start": v(-1111.22, 757.04) * mm, "end": v(-1111.22, 782.44) * mm});
            skLineSegment(sketch, "E326", {"start": v(-1166.34, 757.04) * mm, "end": v(-1063.21, 757.04) * mm});
            skLineSegment(sketch, "E327", {"start": v(-1063.21, 782.44) * mm, "end": v(-1166.34, 782.44) * mm});
            skLineSegment(sketch, "E328", {"start": v(-1127.14, 744.68) * mm, "end": v(-1102.41, 769.4) * mm});
            skLineSegment(sketch, "E329", {"start": v(-1127.14, 769.4) * mm, "end": v(-1102.41, 744.68) * mm});
            skLineSegment(sketch, "E330", {"start": v(-880.22, 853.97) * mm, "end": v(-854.82, 853.97) * mm});
            skLineSegment(sketch, "E331", {"start": v(-854.82, 862.73) * mm, "end": v(-880.22, 862.73) * mm});
            skLineSegment(sketch, "E332", {"start": v(-880.22, 765.83) * mm, "end": v(-854.82, 765.83) * mm});
            skLineSegment(sketch, "E333", {"start": v(-880.22, 757.07) * mm, "end": v(-854.82, 757.07) * mm});
            skLineSegment(sketch, "E334", {"start": v(-880.22, 862.73) * mm, "end": v(-880.22, 757.07) * mm});
            skLineSegment(sketch, "E335", {"start": v(-854.82, 757.07) * mm, "end": v(-854.82, 862.73) * mm});
            skLineSegment(sketch, "E336", {"start": v(-892.58, 744.7) * mm, "end": v(-867.86, 769.43) * mm});
            skLineSegment(sketch, "E337", {"start": v(-892.58, 769.43) * mm, "end": v(-867.86, 744.7) * mm});
            skLineSegment(sketch, "E338", {"start": v(-683.77, 757.04) * mm, "end": v(-556.77, 757.04) * mm});
            skLineSegment(sketch, "E339", {"start": v(-683.77, 884.3) * mm, "end": v(-556.77, 884.3) * mm});
            skArc(sketch, "E340", {"start": v(-631.27, 766.19) * mm, "mid": v(-625.64, 768.52) * mm, "end": v(-623.31, 774.14) * mm});
            skArc(sketch, "E341", {"start": v(-623.31, 867.2) * mm, "mid": v(-625.64, 872.82) * mm, "end": v(-631.27, 875.15) * mm});
            skLineSegment(sketch, "E342", {"start": v(-623.31, 774.14) * mm, "end": v(-623.31, 867.2) * mm});
            skLineSegment(sketch, "E343", {"start": v(-683.77, 766.19) * mm, "end": v(-631.27, 766.19) * mm});
            skLineSegment(sketch, "E344", {"start": v(-683.77, 757.04) * mm, "end": v(-683.77, 766.19) * mm});
            skLineSegment(sketch, "E345", {"start": v(-683.77, 875.15) * mm, "end": v(-631.27, 875.15) * mm});
            skLineSegment(sketch, "E346", {"start": v(-683.77, 884.3) * mm, "end": v(-683.77, 875.15) * mm});
            skLineSegment(sketch, "E347", {"start": v(-617.22, 774.14) * mm, "end": v(-617.22, 867.2) * mm});
            skLineSegment(sketch, "E348", {"start": v(-609.27, 766.19) * mm, "end": v(-556.77, 766.19) * mm});
            skArc(sketch, "E349", {"start": v(-617.22, 774.14) * mm, "mid": v(-614.89, 768.52) * mm, "end": v(-609.27, 766.19) * mm});
            skLineSegment(sketch, "E350", {"start": v(-556.77, 757.04) * mm, "end": v(-556.77, 766.19) * mm});
            skLineSegment(sketch, "E351", {"start": v(-609.27, 875.15) * mm, "end": v(-556.77, 875.15) * mm});
            skArc(sketch, "E352", {"start": v(-609.27, 875.15) * mm, "mid": v(-614.89, 872.82) * mm, "end": v(-617.22, 867.2) * mm});
            skLineSegment(sketch, "E353", {"start": v(-556.77, 884.3) * mm, "end": v(-556.77, 875.15) * mm});
            skLineSegment(sketch, "E354", {"start": v(-632.63, 744.68) * mm, "end": v(-607.9, 769.4) * mm});
            skLineSegment(sketch, "E355", {"start": v(-632.63, 769.4) * mm, "end": v(-607.9, 744.68) * mm});
            skLineSegment(sketch, "E356", {"start": v(-309.51, 757.04) * mm, "end": v(-309.51, 782.44) * mm});
            skLineSegment(sketch, "E357", {"start": v(-436.51, 782.44) * mm, "end": v(-436.51, 757.04) * mm});
            skLineSegment(sketch, "E358", {"start": v(-376.06, 757.04) * mm, "end": v(-376.06, 782.44) * mm});
            skLineSegment(sketch, "E359", {"start": v(-369.96, 757.04) * mm, "end": v(-369.96, 782.44) * mm});
            skLineSegment(sketch, "E360", {"start": v(-436.51, 757.04) * mm, "end": v(-309.51, 757.04) * mm});
            skLineSegment(sketch, "E361", {"start": v(-309.51, 782.44) * mm, "end": v(-436.51, 782.44) * mm});
            skLineSegment(sketch, "E362", {"start": v(-385.38, 744.68) * mm, "end": v(-360.65, 769.4) * mm});
            skLineSegment(sketch, "E363", {"start": v(-385.38, 769.4) * mm, "end": v(-360.65, 744.68) * mm});
            skLineSegment(sketch, "E364", {"start": v(-138.45, 875.18) * mm, "end": v(-113.05, 875.18) * mm});
            skLineSegment(sketch, "E365", {"start": v(-138.45, 766.21) * mm, "end": v(-113.05, 766.21) * mm});
            skLineSegment(sketch, "E366", {"start": v(-138.45, 757.07) * mm, "end": v(-113.05, 757.07) * mm});
            skLineSegment(sketch, "E367", {"start": v(-138.45, 757.07) * mm, "end": v(-138.45, 875.18) * mm});
            skLineSegment(sketch, "E368", {"start": v(-113.05, 875.18) * mm, "end": v(-113.05, 757.07) * mm});
            skLineSegment(sketch, "E369", {"start": v(-150.8, 744.7) * mm, "end": v(-126.08, 769.43) * mm});
            skLineSegment(sketch, "E370", {"start": v(-150.8, 769.43) * mm, "end": v(-126.08, 744.7) * mm});
            skLineSegment(sketch, "E371", {"start": v(57.61, 757.04) * mm, "end": v(185.38, 757.04) * mm});
            skLineSegment(sketch, "E372", {"start": v(57.61, 887.85) * mm, "end": v(185.38, 887.85) * mm});
            skLineSegment(sketch, "E373", {"start": v(133.1, 767.97) * mm, "end": v(185.38, 767.97) * mm});
            skLineSegment(sketch, "E374", {"start": v(133.1, 876.93) * mm, "end": v(185.38, 876.93) * mm});
            skLineSegment(sketch, "E375", {"start": v(118.07, 776.14) * mm, "end": v(118.07, 868.76) * mm});
            skLineSegment(sketch, "E376", {"start": v(124.92, 776.14) * mm, "end": v(124.92, 868.76) * mm});
            skLineSegment(sketch, "E377", {"start": v(57.61, 767.97) * mm, "end": v(109.9, 767.97) * mm});
            skLineSegment(sketch, "E378", {"start": v(57.61, 757.04) * mm, "end": v(57.61, 767.97) * mm});
            skArc(sketch, "E379", {"start": v(124.92, 776.14) * mm, "mid": v(127.32, 770.36) * mm, "end": v(133.1, 767.97) * mm});
            skArc(sketch, "E380", {"start": v(109.9, 767.97) * mm, "mid": v(115.67, 770.36) * mm, "end": v(118.07, 776.14) * mm});
            skLineSegment(sketch, "E381", {"start": v(57.61, 876.93) * mm, "end": v(109.9, 876.93) * mm});
            skLineSegment(sketch, "E382", {"start": v(57.61, 887.85) * mm, "end": v(57.61, 876.93) * mm});
            skArc(sketch, "E383", {"start": v(133.1, 876.93) * mm, "mid": v(127.32, 874.54) * mm, "end": v(124.92, 868.76) * mm});
            skArc(sketch, "E384", {"start": v(118.07, 868.76) * mm, "mid": v(115.67, 874.54) * mm, "end": v(109.9, 876.93) * mm});
            skLineSegment(sketch, "E385", {"start": v(185.38, 757.04) * mm, "end": v(185.38, 767.97) * mm});
            skLineSegment(sketch, "E386", {"start": v(185.38, 887.85) * mm, "end": v(185.38, 876.93) * mm});
            skLineSegment(sketch, "E387", {"start": v(109.13, 744.68) * mm, "end": v(133.86, 769.4) * mm});
            skLineSegment(sketch, "E388", {"start": v(109.13, 769.4) * mm, "end": v(133.86, 744.68) * mm});
            skLineSegment(sketch, "E389", {"start": v(432.66, 757.07) * mm, "end": v(432.66, 782.47) * mm});
            skLineSegment(sketch, "E390", {"start": v(304.9, 782.47) * mm, "end": v(304.9, 757.07) * mm});
            skLineSegment(sketch, "E391", {"start": v(365.35, 757.07) * mm, "end": v(365.35, 782.47) * mm});
            skLineSegment(sketch, "E392", {"start": v(372.2, 757.07) * mm, "end": v(372.2, 782.47) * mm});
            skLineSegment(sketch, "E393", {"start": v(304.9, 757.07) * mm, "end": v(432.66, 757.07) * mm});
            skLineSegment(sketch, "E394", {"start": v(432.66, 782.47) * mm, "end": v(304.9, 782.47) * mm});
            skLineSegment(sketch, "E395", {"start": v(356.41, 744.7) * mm, "end": v(381.14, 769.43) * mm});
            skLineSegment(sketch, "E396", {"start": v(356.41, 769.43) * mm, "end": v(381.14, 744.7) * mm});
            skLineSegment(sketch, "E397", {"start": v(603.33, 767.97) * mm, "end": v(628.73, 767.97) * mm});
            skLineSegment(sketch, "E398", {"start": v(603.33, 757.04) * mm, "end": v(628.73, 757.04) * mm});
            skLineSegment(sketch, "E399", {"start": v(603.33, 876.93) * mm, "end": v(628.73, 876.93) * mm});
            skLineSegment(sketch, "E400", {"start": v(628.73, 887.85) * mm, "end": v(603.33, 887.85) * mm});
            skLineSegment(sketch, "E401", {"start": v(603.33, 887.85) * mm, "end": v(603.33, 757.04) * mm});
            skLineSegment(sketch, "E402", {"start": v(628.73, 757.04) * mm, "end": v(628.73, 887.85) * mm});
            skLineSegment(sketch, "E403", {"start": v(590.97, 744.68) * mm, "end": v(615.7, 769.4) * mm});
            skLineSegment(sketch, "E404", {"start": v(590.97, 769.4) * mm, "end": v(615.7, 744.68) * mm});
            skLineSegment(sketch, "E405", {"start": v(813.22, 757.04) * mm, "end": v(913.3, 757.04) * mm});
            skLineSegment(sketch, "E406", {"start": v(813.22, 906.9) * mm, "end": v(913.3, 906.9) * mm});
            skLineSegment(sketch, "E407", {"start": v(874.78, 762.5) * mm, "end": v(913.3, 762.5) * mm});
            skLineSegment(sketch, "E408", {"start": v(874.78, 901.44) * mm, "end": v(913.3, 901.44) * mm});
            skLineSegment(sketch, "E409", {"start": v(861.1, 771.87) * mm, "end": v(861.1, 892.08) * mm});
            skLineSegment(sketch, "E410", {"start": v(865.42, 771.87) * mm, "end": v(865.42, 892.08) * mm});
            skLineSegment(sketch, "E411", {"start": v(813.22, 762.5) * mm, "end": v(851.73, 762.5) * mm});
            skLineSegment(sketch, "E412", {"start": v(813.22, 757.04) * mm, "end": v(813.22, 762.5) * mm});
            skArc(sketch, "E413", {"start": v(851.73, 762.5) * mm, "mid": v(858.35, 765.25) * mm, "end": v(861.1, 771.87) * mm});
            skArc(sketch, "E414", {"start": v(865.42, 771.87) * mm, "mid": v(868.16, 765.25) * mm, "end": v(874.78, 762.5) * mm});
            skLineSegment(sketch, "E415", {"start": v(813.22, 901.44) * mm, "end": v(851.73, 901.44) * mm});
            skLineSegment(sketch, "E416", {"start": v(813.22, 906.9) * mm, "end": v(813.22, 901.44) * mm});
            skArc(sketch, "E417", {"start": v(861.1, 892.08) * mm, "mid": v(858.35, 898.7) * mm, "end": v(851.73, 901.44) * mm});
            skArc(sketch, "E418", {"start": v(874.78, 901.44) * mm, "mid": v(868.16, 898.7) * mm, "end": v(865.42, 892.08) * mm});
            skLineSegment(sketch, "E419", {"start": v(913.3, 757.04) * mm, "end": v(913.3, 762.5) * mm});
            skLineSegment(sketch, "E420", {"start": v(913.3, 906.9) * mm, "end": v(913.3, 901.44) * mm});
            skLineSegment(sketch, "E421", {"start": v(850.9, 744.68) * mm, "end": v(875.62, 769.4) * mm});
            skLineSegment(sketch, "E422", {"start": v(850.9, 769.4) * mm, "end": v(875.62, 744.68) * mm});
            skLineSegment(sketch, "E423", {"start": v(1160.55, 757.07) * mm, "end": v(1160.55, 782.47) * mm});
            skLineSegment(sketch, "E424", {"start": v(1060.47, 782.47) * mm, "end": v(1060.47, 757.07) * mm});
            skLineSegment(sketch, "E425", {"start": v(1108.35, 757.07) * mm, "end": v(1108.35, 782.47) * mm});
            skLineSegment(sketch, "E426", {"start": v(1112.67, 757.07) * mm, "end": v(1112.67, 782.47) * mm});
            skLineSegment(sketch, "E427", {"start": v(1060.47, 757.07) * mm, "end": v(1160.55, 757.07) * mm});
            skLineSegment(sketch, "E428", {"start": v(1160.55, 782.47) * mm, "end": v(1060.47, 782.47) * mm});
            skLineSegment(sketch, "E429", {"start": v(1098.15, 744.7) * mm, "end": v(1122.87, 769.43) * mm});
            skLineSegment(sketch, "E430", {"start": v(1098.15, 769.43) * mm, "end": v(1122.87, 744.7) * mm});
            skLineSegment(sketch, "E431", {"start": v(1345.08, 901.44) * mm, "end": v(1370.48, 901.44) * mm});
            skLineSegment(sketch, "E432", {"start": v(1370.48, 906.9) * mm, "end": v(1345.08, 906.9) * mm});
            skLineSegment(sketch, "E433", {"start": v(1345.08, 762.5) * mm, "end": v(1370.48, 762.5) * mm});
            skLineSegment(sketch, "E434", {"start": v(1345.08, 757.04) * mm, "end": v(1370.48, 757.04) * mm});
            skLineSegment(sketch, "E435", {"start": v(1345.08, 906.9) * mm, "end": v(1345.08, 757.04) * mm});
            skLineSegment(sketch, "E436", {"start": v(1370.48, 757.04) * mm, "end": v(1370.48, 906.9) * mm});
            skLineSegment(sketch, "E437", {"start": v(1332.71, 744.68) * mm, "end": v(1357.44, 769.4) * mm});
            skLineSegment(sketch, "E438", {"start": v(1332.71, 769.4) * mm, "end": v(1357.44, 744.68) * mm});
            skLineSegment(sketch, "E439", {"start": v(-1364.92, 403.38) * mm, "end": v(-1364.92, 523.18) * mm});
            skLineSegment(sketch, "E440", {"start": v(-1359.08, 403.38) * mm, "end": v(-1359.08, 523.18) * mm});
            skLineSegment(sketch, "E441", {"start": v(-1412.8, 386.7) * mm, "end": v(-1311.2, 386.7) * mm});
            skLineSegment(sketch, "E442", {"start": v(-1412.8, 393.81) * mm, "end": v(-1374.5, 393.81) * mm});
            skLineSegment(sketch, "E443", {"start": v(-1412.8, 386.7) * mm, "end": v(-1412.8, 393.81) * mm});
            skArc(sketch, "E444", {"start": v(-1359.08, 403.38) * mm, "mid": v(-1356.28, 396.61) * mm, "end": v(-1349.5, 393.81) * mm});
            skArc(sketch, "E445", {"start": v(-1374.5, 393.81) * mm, "mid": v(-1367.73, 396.61) * mm, "end": v(-1364.92, 403.38) * mm});
            skLineSegment(sketch, "E446", {"start": v(-1349.5, 393.81) * mm, "end": v(-1311.2, 393.81) * mm});
            skLineSegment(sketch, "E447", {"start": v(-1311.2, 386.7) * mm, "end": v(-1311.2, 393.81) * mm});
            skLineSegment(sketch, "E448", {"start": v(-1412.8, 539.86) * mm, "end": v(-1311.2, 539.86) * mm});
            skLineSegment(sketch, "E449", {"start": v(-1412.8, 532.75) * mm, "end": v(-1374.5, 532.75) * mm});
            skLineSegment(sketch, "E450", {"start": v(-1412.8, 539.86) * mm, "end": v(-1412.8, 532.75) * mm});
            skArc(sketch, "E451", {"start": v(-1349.5, 532.75) * mm, "mid": v(-1356.28, 529.95) * mm, "end": v(-1359.08, 523.18) * mm});
            skArc(sketch, "E452", {"start": v(-1364.92, 523.18) * mm, "mid": v(-1367.73, 529.95) * mm, "end": v(-1374.5, 532.75) * mm});
            skLineSegment(sketch, "E453", {"start": v(-1349.5, 532.75) * mm, "end": v(-1311.2, 532.75) * mm});
            skLineSegment(sketch, "E454", {"start": v(-1311.2, 539.86) * mm, "end": v(-1311.2, 532.75) * mm});
            skLineSegment(sketch, "E455", {"start": v(-1374.36, 374.34) * mm, "end": v(-1349.64, 399.06) * mm});
            skLineSegment(sketch, "E456", {"start": v(-1374.36, 399.06) * mm, "end": v(-1349.64, 374.34) * mm});
            skLineSegment(sketch, "E457", {"start": v(-1064.72, 386.72) * mm, "end": v(-1064.72, 412.12) * mm});
            skLineSegment(sketch, "E458", {"start": v(-1164.8, 412.12) * mm, "end": v(-1164.8, 386.72) * mm});
            skLineSegment(sketch, "E459", {"start": v(-1117.68, 386.72) * mm, "end": v(-1117.68, 412.12) * mm});
            skLineSegment(sketch, "E460", {"start": v(-1111.84, 386.72) * mm, "end": v(-1111.84, 412.12) * mm});
            skLineSegment(sketch, "E461", {"start": v(-1164.8, 386.72) * mm, "end": v(-1064.72, 386.72) * mm});
            skLineSegment(sketch, "E462", {"start": v(-1064.72, 412.12) * mm, "end": v(-1164.8, 412.12) * mm});
            skLineSegment(sketch, "E463", {"start": v(-1127.12, 374.36) * mm, "end": v(-1102.4, 399.09) * mm});
            skLineSegment(sketch, "E464", {"start": v(-1127.12, 399.09) * mm, "end": v(-1102.4, 374.36) * mm});
            skLineSegment(sketch, "E465", {"start": v(-880.2, 539.6) * mm, "end": v(-854.8, 539.6) * mm});
            skLineSegment(sketch, "E466", {"start": v(-854.8, 546.72) * mm, "end": v(-880.2, 546.72) * mm});
            skLineSegment(sketch, "E467", {"start": v(-880.2, 393.81) * mm, "end": v(-854.8, 393.81) * mm});
            skLineSegment(sketch, "E468", {"start": v(-880.2, 386.7) * mm, "end": v(-854.8, 386.7) * mm});
            skLineSegment(sketch, "E469", {"start": v(-880.2, 546.72) * mm, "end": v(-880.2, 386.7) * mm});
            skLineSegment(sketch, "E470", {"start": v(-854.8, 386.7) * mm, "end": v(-854.8, 546.72) * mm});
            skLineSegment(sketch, "E471", {"start": v(-892.57, 374.34) * mm, "end": v(-867.84, 399.06) * mm});
            skLineSegment(sketch, "E472", {"start": v(-892.57, 399.06) * mm, "end": v(-867.84, 374.34) * mm});
            skLineSegment(sketch, "E473", {"start": v(-696.33, 386.7) * mm, "end": v(-544.18, 386.7) * mm});
            skLineSegment(sketch, "E474", {"start": v(-696.33, 538.85) * mm, "end": v(-544.18, 538.85) * mm});
            skLineSegment(sketch, "E475", {"start": v(-607.82, 393.3) * mm, "end": v(-544.18, 393.3) * mm});
            skLineSegment(sketch, "E476", {"start": v(-607.82, 532.24) * mm, "end": v(-544.18, 532.24) * mm});
            skLineSegment(sketch, "E477", {"start": v(-623.17, 402.81) * mm, "end": v(-623.17, 522.73) * mm});
            skLineSegment(sketch, "E478", {"start": v(-617.33, 402.81) * mm, "end": v(-617.33, 522.73) * mm});
            skLineSegment(sketch, "E479", {"start": v(-696.33, 393.3) * mm, "end": v(-632.68, 393.3) * mm});
            skLineSegment(sketch, "E480", {"start": v(-696.33, 386.7) * mm, "end": v(-696.33, 393.3) * mm});
            skArc(sketch, "E481", {"start": v(-632.68, 393.3) * mm, "mid": v(-625.96, 396.09) * mm, "end": v(-623.17, 402.81) * mm});
            skArc(sketch, "E482", {"start": v(-617.33, 402.81) * mm, "mid": v(-614.55, 396.09) * mm, "end": v(-607.82, 393.3) * mm});
            skLineSegment(sketch, "E483", {"start": v(-696.33, 532.24) * mm, "end": v(-632.68, 532.24) * mm});
            skLineSegment(sketch, "E484", {"start": v(-696.33, 538.85) * mm, "end": v(-696.33, 532.24) * mm});
            skArc(sketch, "E485", {"start": v(-623.17, 522.73) * mm, "mid": v(-625.96, 529.46) * mm, "end": v(-632.68, 532.24) * mm});
            skArc(sketch, "E486", {"start": v(-607.82, 532.24) * mm, "mid": v(-614.55, 529.46) * mm, "end": v(-617.33, 522.73) * mm});
            skLineSegment(sketch, "E487", {"start": v(-544.18, 386.7) * mm, "end": v(-544.18, 393.3) * mm});
            skLineSegment(sketch, "E488", {"start": v(-544.18, 538.85) * mm, "end": v(-544.18, 532.24) * mm});
            skLineSegment(sketch, "E489", {"start": v(-632.62, 374.34) * mm, "end": v(-607.9, 399.06) * mm});
            skLineSegment(sketch, "E490", {"start": v(-632.62, 399.06) * mm, "end": v(-607.9, 374.34) * mm});
            skLineSegment(sketch, "E491", {"start": v(-296.93, 386.72) * mm, "end": v(-296.93, 412.12) * mm});
            skLineSegment(sketch, "E492", {"start": v(-449.07, 412.12) * mm, "end": v(-449.07, 386.72) * mm});
            skLineSegment(sketch, "E493", {"start": v(-375.92, 386.72) * mm, "end": v(-375.92, 412.12) * mm});
            skLineSegment(sketch, "E494", {"start": v(-370.08, 386.72) * mm, "end": v(-370.08, 412.12) * mm});
            skLineSegment(sketch, "E495", {"start": v(-449.07, 386.72) * mm, "end": v(-296.93, 386.72) * mm});
            skLineSegment(sketch, "E496", {"start": v(-296.93, 412.12) * mm, "end": v(-449.07, 412.12) * mm});
            skLineSegment(sketch, "E497", {"start": v(-385.36, 374.36) * mm, "end": v(-360.64, 399.09) * mm});
            skLineSegment(sketch, "E498", {"start": v(-385.36, 399.09) * mm, "end": v(-360.64, 374.36) * mm});
            skLineSegment(sketch, "E499", {"start": v(-113.03, 538.85) * mm, "end": v(-138.43, 538.85) * mm});
            skLineSegment(sketch, "E500", {"start": v(-138.43, 532.24) * mm, "end": v(-113.03, 532.24) * mm});
            skLineSegment(sketch, "E501", {"start": v(-138.43, 386.7) * mm, "end": v(-113.03, 386.7) * mm});
            skLineSegment(sketch, "E502", {"start": v(-138.43, 393.3) * mm, "end": v(-113.03, 393.3) * mm});
            skLineSegment(sketch, "E503", {"start": v(-138.43, 538.85) * mm, "end": v(-138.43, 386.7) * mm});
            skLineSegment(sketch, "E504", {"start": v(-113.03, 386.7) * mm, "end": v(-113.03, 538.85) * mm});
            skLineSegment(sketch, "E505", {"start": v(-150.8, 374.34) * mm, "end": v(-126.07, 399.06) * mm});
            skLineSegment(sketch, "E506", {"start": v(-150.8, 399.06) * mm, "end": v(-126.07, 374.34) * mm});
            skLineSegment(sketch, "E507", {"start": v(70.31, 386.7) * mm, "end": v(172.68, 386.7) * mm});
            skLineSegment(sketch, "E508", {"start": v(70.31, 546.21) * mm, "end": v(172.68, 546.21) * mm});
            skLineSegment(sketch, "E509", {"start": v(134.77, 396.99) * mm, "end": v(172.68, 396.99) * mm});
            skLineSegment(sketch, "E510", {"start": v(134.77, 535.92) * mm, "end": v(172.68, 535.92) * mm});
            skLineSegment(sketch, "E511", {"start": v(118.2, 406.96) * mm, "end": v(118.2, 525.95) * mm});
            skLineSegment(sketch, "E512", {"start": v(124.8, 406.96) * mm, "end": v(124.8, 525.95) * mm});
            skLineSegment(sketch, "E513", {"start": v(70.31, 396.99) * mm, "end": v(108.22, 396.99) * mm});
            skLineSegment(sketch, "E514", {"start": v(70.31, 386.7) * mm, "end": v(70.31, 396.99) * mm});
            skArc(sketch, "E515", {"start": v(124.8, 406.96) * mm, "mid": v(127.72, 399.9) * mm, "end": v(134.77, 396.99) * mm});
            skArc(sketch, "E516", {"start": v(108.22, 396.99) * mm, "mid": v(115.27, 399.9) * mm, "end": v(118.2, 406.96) * mm});
            skLineSegment(sketch, "E517", {"start": v(70.31, 535.92) * mm, "end": v(108.22, 535.92) * mm});
            skLineSegment(sketch, "E518", {"start": v(70.31, 546.21) * mm, "end": v(70.31, 535.92) * mm});
            skArc(sketch, "E519", {"start": v(134.77, 535.92) * mm, "mid": v(127.72, 533) * mm, "end": v(124.8, 525.95) * mm});
            skArc(sketch, "E520", {"start": v(118.2, 525.95) * mm, "mid": v(115.27, 533) * mm, "end": v(108.22, 535.92) * mm});
            skLineSegment(sketch, "E521", {"start": v(172.68, 386.7) * mm, "end": v(172.68, 396.99) * mm});
            skLineSegment(sketch, "E522", {"start": v(172.68, 546.21) * mm, "end": v(172.68, 535.92) * mm});
            skLineSegment(sketch, "E523", {"start": v(109.13, 374.34) * mm, "end": v(133.86, 399.06) * mm});
            skLineSegment(sketch, "E524", {"start": v(109.13, 399.06) * mm, "end": v(133.86, 374.34) * mm});
            skLineSegment(sketch, "E525", {"start": v(419.95, 386.72) * mm, "end": v(419.95, 412.12) * mm});
            skLineSegment(sketch, "E526", {"start": v(365.47, 386.72) * mm, "end": v(365.47, 412.12) * mm});
            skLineSegment(sketch, "E527", {"start": v(372.08, 386.72) * mm, "end": v(372.08, 412.12) * mm});
            skLineSegment(sketch, "E528", {"start": v(317.6, 412.12) * mm, "end": v(317.6, 386.72) * mm});
            skLineSegment(sketch, "E529", {"start": v(317.6, 386.72) * mm, "end": v(419.95, 386.72) * mm});
            skLineSegment(sketch, "E530", {"start": v(419.95, 412.12) * mm, "end": v(317.6, 412.12) * mm});
            skLineSegment(sketch, "E531", {"start": v(356.41, 374.36) * mm, "end": v(381.14, 399.09) * mm});
            skLineSegment(sketch, "E532", {"start": v(356.41, 399.09) * mm, "end": v(381.14, 374.36) * mm});
            skLineSegment(sketch, "E533", {"start": v(628.72, 546.21) * mm, "end": v(603.32, 546.21) * mm});
            skLineSegment(sketch, "E534", {"start": v(603.32, 535.92) * mm, "end": v(628.72, 535.92) * mm});
            skLineSegment(sketch, "E535", {"start": v(603.32, 396.99) * mm, "end": v(628.72, 396.99) * mm});
            skLineSegment(sketch, "E536", {"start": v(603.32, 386.7) * mm, "end": v(628.72, 386.7) * mm});
            skLineSegment(sketch, "E537", {"start": v(603.32, 546.21) * mm, "end": v(603.32, 386.7) * mm});
            skLineSegment(sketch, "E538", {"start": v(628.72, 386.7) * mm, "end": v(628.72, 546.21) * mm});
            skLineSegment(sketch, "E539", {"start": v(590.95, 374.34) * mm, "end": v(615.68, 399.06) * mm});
            skLineSegment(sketch, "E540", {"start": v(590.95, 399.06) * mm, "end": v(615.68, 374.34) * mm});
            skLineSegment(sketch, "E541", {"start": v(786.81, 386.7) * mm, "end": v(939.72, 386.7) * mm});
            skLineSegment(sketch, "E542", {"start": v(786.81, 544.18) * mm, "end": v(939.72, 544.18) * mm});
            skLineSegment(sketch, "E543", {"start": v(876.41, 395.97) * mm, "end": v(939.72, 395.97) * mm});
            skLineSegment(sketch, "E544", {"start": v(876.41, 534.9) * mm, "end": v(939.72, 534.9) * mm});
            skLineSegment(sketch, "E545", {"start": v(859.97, 405.81) * mm, "end": v(859.97, 525.07) * mm});
            skLineSegment(sketch, "E546", {"start": v(866.57, 405.81) * mm, "end": v(866.57, 525.07) * mm});
            skLineSegment(sketch, "E547", {"start": v(786.81, 395.97) * mm, "end": v(850.12, 395.97) * mm});
            skLineSegment(sketch, "E548", {"start": v(786.81, 386.7) * mm, "end": v(786.81, 395.97) * mm});
            skArc(sketch, "E549", {"start": v(850.12, 395.97) * mm, "mid": v(857.08, 398.85) * mm, "end": v(859.97, 405.81) * mm});
            skArc(sketch, "E550", {"start": v(866.57, 405.81) * mm, "mid": v(869.45, 398.85) * mm, "end": v(876.41, 395.97) * mm});
            skLineSegment(sketch, "E551", {"start": v(786.81, 534.9) * mm, "end": v(850.12, 534.9) * mm});
            skLineSegment(sketch, "E552", {"start": v(786.81, 544.18) * mm, "end": v(786.81, 534.9) * mm});
            skArc(sketch, "E553", {"start": v(859.97, 525.07) * mm, "mid": v(857.08, 532.03) * mm, "end": v(850.12, 534.9) * mm});
            skArc(sketch, "E554", {"start": v(876.41, 534.9) * mm, "mid": v(869.45, 532.03) * mm, "end": v(866.57, 525.07) * mm});
            skLineSegment(sketch, "E555", {"start": v(939.72, 386.7) * mm, "end": v(939.72, 395.97) * mm});
            skLineSegment(sketch, "E556", {"start": v(939.72, 544.18) * mm, "end": v(939.72, 534.9) * mm});
            skLineSegment(sketch, "E557", {"start": v(850.9, 374.34) * mm, "end": v(875.63, 399.06) * mm});
            skLineSegment(sketch, "E558", {"start": v(850.9, 399.06) * mm, "end": v(875.63, 374.34) * mm});
            skLineSegment(sketch, "E559", {"start": v(1186.58, 412.12) * mm, "end": v(1034.44, 412.12) * mm});
            skLineSegment(sketch, "E560", {"start": v(1034.44, 386.72) * mm, "end": v(1186.58, 386.72) * mm});
            skLineSegment(sketch, "E561", {"start": v(1034.44, 412.12) * mm, "end": v(1034.44, 386.72) * mm});
            skLineSegment(sketch, "E562", {"start": v(1186.58, 386.72) * mm, "end": v(1186.58, 412.12) * mm});
            skLineSegment(sketch, "E563", {"start": v(1107.2, 386.72) * mm, "end": v(1107.2, 412.12) * mm});
            skLineSegment(sketch, "E564", {"start": v(1113.81, 386.72) * mm, "end": v(1113.81, 412.12) * mm});
            skLineSegment(sketch, "E565", {"start": v(1098.15, 374.36) * mm, "end": v(1122.87, 399.09) * mm});
            skLineSegment(sketch, "E566", {"start": v(1098.15, 399.09) * mm, "end": v(1122.87, 374.36) * mm});
            skLineSegment(sketch, "E567", {"start": v(1370.46, 386.7) * mm, "end": v(1370.46, 544.18) * mm});
            skLineSegment(sketch, "E568", {"start": v(1345.06, 544.18) * mm, "end": v(1345.06, 386.7) * mm});
            skLineSegment(sketch, "E569", {"start": v(1345.06, 395.97) * mm, "end": v(1370.46, 395.97) * mm});
            skLineSegment(sketch, "E570", {"start": v(1345.06, 386.7) * mm, "end": v(1370.46, 386.7) * mm});
            skLineSegment(sketch, "E571", {"start": v(1345.06, 534.9) * mm, "end": v(1370.46, 534.9) * mm});
            skLineSegment(sketch, "E572", {"start": v(1370.46, 544.18) * mm, "end": v(1345.06, 544.18) * mm});
            skLineSegment(sketch, "E573", {"start": v(1332.7, 374.34) * mm, "end": v(1357.43, 399.06) * mm});
            skLineSegment(sketch, "E574", {"start": v(1332.7, 399.06) * mm, "end": v(1357.43, 374.34) * mm});
            skLineSegment(sketch, "E575", {"start": v(-1439.24, 16.35) * mm, "end": v(-1284.81, 16.35) * mm});
            skLineSegment(sketch, "E576", {"start": v(-1439.24, 178.4) * mm, "end": v(-1284.81, 178.4) * mm});
            skArc(sketch, "E577", {"start": v(-1357.96, 38.04) * mm, "mid": v(-1355, 30.88) * mm, "end": v(-1347.84, 27.91) * mm});
            skArc(sketch, "E578", {"start": v(-1347.84, 166.85) * mm, "mid": v(-1355, 163.88) * mm, "end": v(-1357.96, 156.72) * mm});
            skLineSegment(sketch, "E579", {"start": v(-1366.1, 38.04) * mm, "end": v(-1366.1, 156.72) * mm});
            skLineSegment(sketch, "E580", {"start": v(-1357.96, 38.04) * mm, "end": v(-1357.96, 156.72) * mm});
            skLineSegment(sketch, "E581", {"start": v(-1439.24, 27.91) * mm, "end": v(-1376.22, 27.91) * mm});
            skLineSegment(sketch, "E582", {"start": v(-1439.24, 16.35) * mm, "end": v(-1439.24, 27.91) * mm});
            skArc(sketch, "E583", {"start": v(-1376.22, 27.91) * mm, "mid": v(-1369.06, 30.88) * mm, "end": v(-1366.1, 38.04) * mm});
            skLineSegment(sketch, "E584", {"start": v(-1439.24, 166.85) * mm, "end": v(-1376.22, 166.85) * mm});
            skLineSegment(sketch, "E585", {"start": v(-1439.24, 178.4) * mm, "end": v(-1439.24, 166.85) * mm});
            skArc(sketch, "E586", {"start": v(-1366.1, 156.72) * mm, "mid": v(-1369.06, 163.88) * mm, "end": v(-1376.22, 166.85) * mm});
            skLineSegment(sketch, "E587", {"start": v(-1347.84, 27.91) * mm, "end": v(-1284.81, 27.91) * mm});
            skLineSegment(sketch, "E588", {"start": v(-1284.81, 16.35) * mm, "end": v(-1284.81, 27.91) * mm});
            skLineSegment(sketch, "E589", {"start": v(-1347.84, 166.85) * mm, "end": v(-1284.81, 166.85) * mm});
            skLineSegment(sketch, "E590", {"start": v(-1284.81, 178.4) * mm, "end": v(-1284.81, 166.85) * mm});
            skLineSegment(sketch, "E591", {"start": v(-1374.4, 4) * mm, "end": v(-1349.67, 28.72) * mm});
            skLineSegment(sketch, "E592", {"start": v(-1374.4, 28.72) * mm, "end": v(-1349.67, 4) * mm});
            skLineSegment(sketch, "E593", {"start": v(-1037.55, 41.78) * mm, "end": v(-1191.98, 41.78) * mm});
            skLineSegment(sketch, "E594", {"start": v(-1191.98, 16.38) * mm, "end": v(-1037.55, 16.38) * mm});
            skLineSegment(sketch, "E595", {"start": v(-1191.98, 41.78) * mm, "end": v(-1191.98, 16.38) * mm});
            skLineSegment(sketch, "E596", {"start": v(-1037.55, 16.38) * mm, "end": v(-1037.55, 41.78) * mm});
            skLineSegment(sketch, "E597", {"start": v(-1118.83, 16.38) * mm, "end": v(-1118.83, 41.78) * mm});
            skLineSegment(sketch, "E598", {"start": v(-1110.7, 16.38) * mm, "end": v(-1110.7, 41.78) * mm});
            skLineSegment(sketch, "E599", {"start": v(-1127.12, 4.02) * mm, "end": v(-1102.4, 28.74) * mm});
            skLineSegment(sketch, "E600", {"start": v(-1127.12, 28.74) * mm, "end": v(-1102.4, 4.02) * mm});
            skLineSegment(sketch, "E601", {"start": v(-880.2, 166.85) * mm, "end": v(-854.8, 166.85) * mm});
            skLineSegment(sketch, "E602", {"start": v(-854.8, 178.4) * mm, "end": v(-880.2, 178.4) * mm});
            skLineSegment(sketch, "E603", {"start": v(-880.2, 27.91) * mm, "end": v(-854.8, 27.91) * mm});
            skLineSegment(sketch, "E604", {"start": v(-880.2, 16.35) * mm, "end": v(-854.8, 16.35) * mm});
            skLineSegment(sketch, "E605", {"start": v(-880.2, 178.4) * mm, "end": v(-880.2, 16.35) * mm});
            skLineSegment(sketch, "E606", {"start": v(-854.8, 16.35) * mm, "end": v(-854.8, 178.4) * mm});
            skLineSegment(sketch, "E607", {"start": v(-892.57, 4) * mm, "end": v(-867.84, 28.72) * mm});
            skLineSegment(sketch, "E608", {"start": v(-892.57, 28.72) * mm, "end": v(-867.84, 4) * mm});
            skLineSegment(sketch, "E609", {"start": v(-670.3, 16.38) * mm, "end": v(-570.22, 16.38) * mm});
            skLineSegment(sketch, "E610", {"start": v(-670.3, 216.79) * mm, "end": v(-570.22, 216.79) * mm});
            skLineSegment(sketch, "E611", {"start": v(-605.57, 21.59) * mm, "end": v(-570.22, 21.59) * mm});
            skLineSegment(sketch, "E612", {"start": v(-605.57, 211.58) * mm, "end": v(-570.22, 211.58) * mm});
            skLineSegment(sketch, "E613", {"start": v(-622.41, 34.11) * mm, "end": v(-622.41, 199.05) * mm});
            skLineSegment(sketch, "E614", {"start": v(-618.1, 34.11) * mm, "end": v(-618.1, 199.05) * mm});
            skLineSegment(sketch, "E615", {"start": v(-670.3, 21.59) * mm, "end": v(-634.94, 21.59) * mm});
            skLineSegment(sketch, "E616", {"start": v(-670.3, 16.38) * mm, "end": v(-670.3, 21.59) * mm});
            skArc(sketch, "E617", {"start": v(-634.94, 21.59) * mm, "mid": v(-626.08, 25.26) * mm, "end": v(-622.41, 34.11) * mm});
            skArc(sketch, "E618", {"start": v(-618.1, 34.11) * mm, "mid": v(-614.43, 25.26) * mm, "end": v(-605.57, 21.59) * mm});
            skLineSegment(sketch, "E619", {"start": v(-670.3, 211.58) * mm, "end": v(-634.94, 211.58) * mm});
            skLineSegment(sketch, "E620", {"start": v(-670.3, 216.79) * mm, "end": v(-670.3, 211.58) * mm});
            skArc(sketch, "E621", {"start": v(-622.41, 199.05) * mm, "mid": v(-626.08, 207.91) * mm, "end": v(-634.94, 211.58) * mm});
            skArc(sketch, "E622", {"start": v(-605.57, 211.58) * mm, "mid": v(-614.43, 207.91) * mm, "end": v(-618.1, 199.05) * mm});
            skLineSegment(sketch, "E623", {"start": v(-570.22, 16.38) * mm, "end": v(-570.22, 21.59) * mm});
            skLineSegment(sketch, "E624", {"start": v(-570.22, 216.79) * mm, "end": v(-570.22, 211.58) * mm});
            skLineSegment(sketch, "E625", {"start": v(-632.62, 4.02) * mm, "end": v(-607.9, 28.74) * mm});
            skLineSegment(sketch, "E626", {"start": v(-632.62, 28.74) * mm, "end": v(-607.9, 4.02) * mm});
            skLineSegment(sketch, "E627", {"start": v(-322.96, 16.35) * mm, "end": v(-322.96, 41.75) * mm});
            skLineSegment(sketch, "E628", {"start": v(-423.04, 41.75) * mm, "end": v(-423.04, 16.35) * mm});
            skLineSegment(sketch, "E629", {"start": v(-375.16, 16.35) * mm, "end": v(-375.16, 41.75) * mm});
            skLineSegment(sketch, "E630", {"start": v(-370.84, 16.35) * mm, "end": v(-370.84, 41.75) * mm});
            skLineSegment(sketch, "E631", {"start": v(-423.04, 16.35) * mm, "end": v(-322.96, 16.35) * mm});
            skLineSegment(sketch, "E632", {"start": v(-322.96, 41.75) * mm, "end": v(-423.04, 41.75) * mm});
            skLineSegment(sketch, "E633", {"start": v(-385.36, 4) * mm, "end": v(-360.64, 28.72) * mm});
            skLineSegment(sketch, "E634", {"start": v(-385.36, 28.72) * mm, "end": v(-360.64, 4) * mm});
            skLineSegment(sketch, "E635", {"start": v(-113.05, 16.35) * mm, "end": v(-113.05, 216.76) * mm});
            skLineSegment(sketch, "E636", {"start": v(-138.45, 216.76) * mm, "end": v(-138.45, 16.35) * mm});
            skLineSegment(sketch, "E637", {"start": v(-138.45, 16.35) * mm, "end": v(-113.05, 16.35) * mm});
            skLineSegment(sketch, "E638", {"start": v(-138.45, 21.56) * mm, "end": v(-113.05, 21.56) * mm});
            skLineSegment(sketch, "E639", {"start": v(-113.05, 216.76) * mm, "end": v(-138.45, 216.76) * mm});
            skLineSegment(sketch, "E640", {"start": v(-138.45, 211.55) * mm, "end": v(-113.05, 211.55) * mm});
            skLineSegment(sketch, "E641", {"start": v(-150.8, 4) * mm, "end": v(-126.08, 28.72) * mm});
            skLineSegment(sketch, "E642", {"start": v(-150.8, 28.72) * mm, "end": v(-126.08, 4) * mm});
            skLineSegment(sketch, "E643", {"start": v(70.72, 16.35) * mm, "end": v(172.32, 16.35) * mm});
            skLineSegment(sketch, "E644", {"start": v(70.72, 219.3) * mm, "end": v(172.32, 219.3) * mm});
            skLineSegment(sketch, "E645", {"start": v(137.13, 22.83) * mm, "end": v(172.32, 22.83) * mm});
            skLineSegment(sketch, "E646", {"start": v(137.13, 212.82) * mm, "end": v(172.32, 212.82) * mm});
            skLineSegment(sketch, "E647", {"start": v(118.6, 35.52) * mm, "end": v(118.6, 200.14) * mm});
            skLineSegment(sketch, "E648", {"start": v(124.44, 35.52) * mm, "end": v(124.44, 200.14) * mm});
            skArc(sketch, "E649", {"start": v(105.92, 22.83) * mm, "mid": v(114.88, 26.55) * mm, "end": v(118.6, 35.52) * mm});
            skLineSegment(sketch, "E650", {"start": v(70.72, 22.83) * mm, "end": v(105.92, 22.83) * mm});
            skLineSegment(sketch, "E651", {"start": v(70.72, 16.35) * mm, "end": v(70.72, 22.83) * mm});
            skArc(sketch, "E652", {"start": v(124.44, 35.52) * mm, "mid": v(128.16, 26.55) * mm, "end": v(137.13, 22.83) * mm});
            skArc(sketch, "E653", {"start": v(118.6, 200.14) * mm, "mid": v(114.88, 209.1) * mm, "end": v(105.92, 212.82) * mm});
            skArc(sketch, "E654", {"start": v(137.13, 212.82) * mm, "mid": v(128.16, 209.1) * mm, "end": v(124.44, 200.14) * mm});
            skLineSegment(sketch, "E655", {"start": v(70.72, 212.82) * mm, "end": v(105.92, 212.82) * mm});
            skLineSegment(sketch, "E656", {"start": v(70.72, 219.3) * mm, "end": v(70.72, 212.82) * mm});
            skLineSegment(sketch, "E657", {"start": v(172.32, 16.35) * mm, "end": v(172.32, 22.83) * mm});
            skLineSegment(sketch, "E658", {"start": v(172.32, 219.3) * mm, "end": v(172.32, 212.82) * mm});
            skLineSegment(sketch, "E659", {"start": v(109.16, 4) * mm, "end": v(133.88, 28.72) * mm});
            skLineSegment(sketch, "E660", {"start": v(109.16, 28.72) * mm, "end": v(133.88, 4) * mm});
            skLineSegment(sketch, "E661", {"start": v(418.8, 16.38) * mm, "end": v(418.8, 41.78) * mm});
            skLineSegment(sketch, "E662", {"start": v(365.84, 16.38) * mm, "end": v(365.84, 41.78) * mm});
            skLineSegment(sketch, "E663", {"start": v(371.68, 16.38) * mm, "end": v(371.68, 41.78) * mm});
            skLineSegment(sketch, "E664", {"start": v(318.72, 41.78) * mm, "end": v(318.72, 16.38) * mm});
            skLineSegment(sketch, "E665", {"start": v(318.72, 16.38) * mm, "end": v(418.8, 16.38) * mm});
            skLineSegment(sketch, "E666", {"start": v(418.8, 41.78) * mm, "end": v(318.72, 41.78) * mm});
            skLineSegment(sketch, "E667", {"start": v(356.4, 4.02) * mm, "end": v(381.12, 28.74) * mm});
            skLineSegment(sketch, "E668", {"start": v(356.4, 28.74) * mm, "end": v(381.12, 4.02) * mm});
            skLineSegment(sketch, "E669", {"start": v(628.72, 16.35) * mm, "end": v(628.72, 219.3) * mm});
            skLineSegment(sketch, "E670", {"start": v(603.32, 219.3) * mm, "end": v(603.32, 16.35) * mm});
            skLineSegment(sketch, "E671", {"start": v(603.32, 16.35) * mm, "end": v(628.72, 16.35) * mm});
            skLineSegment(sketch, "E672", {"start": v(603.32, 22.83) * mm, "end": v(628.72, 22.83) * mm});
            skLineSegment(sketch, "E673", {"start": v(628.72, 219.3) * mm, "end": v(603.32, 219.3) * mm});
            skLineSegment(sketch, "E674", {"start": v(603.32, 212.82) * mm, "end": v(628.72, 212.82) * mm});
            skLineSegment(sketch, "E675", {"start": v(590.95, 4) * mm, "end": v(615.68, 28.72) * mm});
            skLineSegment(sketch, "E676", {"start": v(590.95, 28.72) * mm, "end": v(615.68, 4) * mm});
            skLineSegment(sketch, "E677", {"start": v(812.28, 16.35) * mm, "end": v(914.26, 16.35) * mm});
            skLineSegment(sketch, "E678", {"start": v(812.28, 222.35) * mm, "end": v(914.26, 222.35) * mm});
            skArc(sketch, "E679", {"start": v(847.28, 24.36) * mm, "mid": v(856.39, 28.13) * mm, "end": v(860.16, 37.23) * mm});
            skArc(sketch, "E680", {"start": v(860.16, 201.47) * mm, "mid": v(856.39, 210.58) * mm, "end": v(847.28, 214.35) * mm});
            skLineSegment(sketch, "E681", {"start": v(860.16, 37.23) * mm, "end": v(860.16, 201.47) * mm});
            skLineSegment(sketch, "E682", {"start": v(812.28, 24.36) * mm, "end": v(847.28, 24.36) * mm});
            skLineSegment(sketch, "E683", {"start": v(812.28, 16.35) * mm, "end": v(812.28, 24.36) * mm});
            skLineSegment(sketch, "E684", {"start": v(812.28, 214.35) * mm, "end": v(847.28, 214.35) * mm});
            skLineSegment(sketch, "E685", {"start": v(812.28, 222.35) * mm, "end": v(812.28, 214.35) * mm});
            skLineSegment(sketch, "E686", {"start": v(866.38, 37.23) * mm, "end": v(866.38, 201.47) * mm});
            skLineSegment(sketch, "E687", {"start": v(879.25, 24.36) * mm, "end": v(914.26, 24.36) * mm});
            skArc(sketch, "E688", {"start": v(866.38, 37.23) * mm, "mid": v(870.15, 28.13) * mm, "end": v(879.25, 24.36) * mm});
            skLineSegment(sketch, "E689", {"start": v(914.26, 16.35) * mm, "end": v(914.26, 24.36) * mm});
            skArc(sketch, "E690", {"start": v(879.25, 214.35) * mm, "mid": v(870.15, 210.58) * mm, "end": v(866.38, 201.47) * mm});
            skLineSegment(sketch, "E691", {"start": v(879.25, 214.35) * mm, "end": v(914.26, 214.35) * mm});
            skLineSegment(sketch, "E692", {"start": v(914.26, 222.35) * mm, "end": v(914.26, 214.35) * mm});
            skLineSegment(sketch, "E693", {"start": v(850.9, 4) * mm, "end": v(875.63, 28.72) * mm});
            skLineSegment(sketch, "E694", {"start": v(850.9, 28.72) * mm, "end": v(875.63, 4) * mm});
            skLineSegment(sketch, "E695", {"start": v(1161.53, 16.38) * mm, "end": v(1161.53, 41.78) * mm});
            skLineSegment(sketch, "E696", {"start": v(1059.54, 41.78) * mm, "end": v(1059.54, 16.38) * mm});
            skLineSegment(sketch, "E697", {"start": v(1107.42, 16.38) * mm, "end": v(1107.42, 41.78) * mm});
            skLineSegment(sketch, "E698", {"start": v(1113.65, 16.38) * mm, "end": v(1113.65, 41.78) * mm});
            skLineSegment(sketch, "E699", {"start": v(1059.54, 16.38) * mm, "end": v(1161.53, 16.38) * mm});
            skLineSegment(sketch, "E700", {"start": v(1161.53, 41.78) * mm, "end": v(1059.54, 41.78) * mm});
            skLineSegment(sketch, "E701", {"start": v(1098.17, 4.02) * mm, "end": v(1122.9, 28.74) * mm});
            skLineSegment(sketch, "E702", {"start": v(1098.17, 28.74) * mm, "end": v(1122.9, 4.02) * mm});
            skLineSegment(sketch, "E703", {"start": v(1345.08, 16.35) * mm, "end": v(1370.48, 16.35) * mm});
            skLineSegment(sketch, "E704", {"start": v(1345.08, 24.36) * mm, "end": v(1370.48, 24.36) * mm});
            skLineSegment(sketch, "E705", {"start": v(1370.48, 222.35) * mm, "end": v(1345.08, 222.35) * mm});
            skLineSegment(sketch, "E706", {"start": v(1345.08, 214.35) * mm, "end": v(1370.48, 214.35) * mm});
            skLineSegment(sketch, "E707", {"start": v(1345.08, 222.35) * mm, "end": v(1345.08, 16.35) * mm});
            skLineSegment(sketch, "E708", {"start": v(1370.48, 16.35) * mm, "end": v(1370.48, 222.35) * mm});
            skLineSegment(sketch, "E709", {"start": v(1332.71, 4) * mm, "end": v(1357.44, 28.72) * mm});
            skLineSegment(sketch, "E710", {"start": v(1332.71, 28.72) * mm, "end": v(1357.44, 4) * mm});
            skLineSegment(sketch, "E711", {"start": v(-1428.7, -353.99) * mm, "end": v(-1295.34, -353.99) * mm});
            skLineSegment(sketch, "E712", {"start": v(-1428.7, -147.23) * mm, "end": v(-1295.34, -147.23) * mm});
            skArc(sketch, "E713", {"start": v(-1377.86, -345.6) * mm, "mid": v(-1368.72, -341.82) * mm, "end": v(-1364.94, -332.69) * mm});
            skArc(sketch, "E714", {"start": v(-1364.94, -168.54) * mm, "mid": v(-1368.72, -159.4) * mm, "end": v(-1377.86, -155.62) * mm});
            skLineSegment(sketch, "E715", {"start": v(-1428.7, -345.6) * mm, "end": v(-1377.86, -345.6) * mm});
            skLineSegment(sketch, "E716", {"start": v(-1428.7, -353.99) * mm, "end": v(-1428.7, -345.6) * mm});
            skLineSegment(sketch, "E717", {"start": v(-1428.7, -155.62) * mm, "end": v(-1377.86, -155.62) * mm});
            skLineSegment(sketch, "E718", {"start": v(-1428.7, -147.23) * mm, "end": v(-1428.7, -155.62) * mm});
            skLineSegment(sketch, "E719", {"start": v(-1364.94, -332.69) * mm, "end": v(-1364.94, -168.54) * mm});
            skLineSegment(sketch, "E720", {"start": v(-1359.1, -332.69) * mm, "end": v(-1359.1, -168.54) * mm});
            skArc(sketch, "E721", {"start": v(-1359.1, -332.69) * mm, "mid": v(-1355.3, -341.82) * mm, "end": v(-1346.17, -345.6) * mm});
            skLineSegment(sketch, "E722", {"start": v(-1346.17, -345.6) * mm, "end": v(-1295.34, -345.6) * mm});
            skLineSegment(sketch, "E723", {"start": v(-1295.34, -353.99) * mm, "end": v(-1295.34, -345.6) * mm});
            skLineSegment(sketch, "E724", {"start": v(-1346.17, -155.62) * mm, "end": v(-1295.34, -155.62) * mm});
            skArc(sketch, "E725", {"start": v(-1346.17, -155.62) * mm, "mid": v(-1355.3, -159.4) * mm, "end": v(-1359.1, -168.54) * mm});
            skLineSegment(sketch, "E726", {"start": v(-1295.34, -147.23) * mm, "end": v(-1295.34, -155.62) * mm});
            skLineSegment(sketch, "E727", {"start": v(-1374.38, -366.35) * mm, "end": v(-1349.65, -341.63) * mm});
            skLineSegment(sketch, "E728", {"start": v(-1374.38, -341.63) * mm, "end": v(-1349.65, -366.35) * mm});
            skLineSegment(sketch, "E729", {"start": v(-1047.9, -353.96) * mm, "end": v(-1047.9, -328.56) * mm});
            skLineSegment(sketch, "E730", {"start": v(-1181.63, -328.56) * mm, "end": v(-1181.63, -353.96) * mm});
            skLineSegment(sketch, "E731", {"start": v(-1117.68, -353.96) * mm, "end": v(-1117.68, -328.56) * mm});
            skLineSegment(sketch, "E732", {"start": v(-1111.84, -353.96) * mm, "end": v(-1111.84, -328.56) * mm});
            skLineSegment(sketch, "E733", {"start": v(-1181.63, -353.96) * mm, "end": v(-1047.9, -353.96) * mm});
            skLineSegment(sketch, "E734", {"start": v(-1047.9, -328.56) * mm, "end": v(-1181.63, -328.56) * mm});
            skLineSegment(sketch, "E735", {"start": v(-1127.12, -366.33) * mm, "end": v(-1102.4, -341.6) * mm});
            skLineSegment(sketch, "E736", {"start": v(-1127.12, -341.6) * mm, "end": v(-1102.4, -366.33) * mm});
            skLineSegment(sketch, "E737", {"start": v(-854.8, -147.23) * mm, "end": v(-880.2, -147.23) * mm});
            skLineSegment(sketch, "E738", {"start": v(-880.2, -155.62) * mm, "end": v(-854.8, -155.62) * mm});
            skLineSegment(sketch, "E739", {"start": v(-880.2, -353.99) * mm, "end": v(-854.8, -353.99) * mm});
            skLineSegment(sketch, "E740", {"start": v(-880.2, -345.6) * mm, "end": v(-854.8, -345.6) * mm});
            skLineSegment(sketch, "E741", {"start": v(-880.2, -147.23) * mm, "end": v(-880.2, -353.99) * mm});
            skLineSegment(sketch, "E742", {"start": v(-854.8, -353.99) * mm, "end": v(-854.8, -147.23) * mm});
            skLineSegment(sketch, "E743", {"start": v(-892.57, -366.35) * mm, "end": v(-867.84, -341.63) * mm});
            skLineSegment(sketch, "E744", {"start": v(-892.57, -341.63) * mm, "end": v(-867.84, -366.35) * mm});
            skLineSegment(sketch, "E745", {"start": v(-687.18, -353.99) * mm, "end": v(-553.32, -353.99) * mm});
            skLineSegment(sketch, "E746", {"start": v(-687.18, -143.68) * mm, "end": v(-553.32, -143.68) * mm});
            skArc(sketch, "E747", {"start": v(-617.08, -330.68) * mm, "mid": v(-613.23, -339.98) * mm, "end": v(-603.93, -343.83) * mm});
            skArc(sketch, "E748", {"start": v(-603.93, -153.84) * mm, "mid": v(-613.23, -157.69) * mm, "end": v(-617.08, -166.98) * mm});
            skLineSegment(sketch, "E749", {"start": v(-623.43, -330.68) * mm, "end": v(-623.43, -166.98) * mm});
            skLineSegment(sketch, "E750", {"start": v(-617.08, -330.68) * mm, "end": v(-617.08, -166.98) * mm});
            skArc(sketch, "E751", {"start": v(-636.57, -343.83) * mm, "mid": v(-627.28, -339.98) * mm, "end": v(-623.43, -330.68) * mm});
            skLineSegment(sketch, "E752", {"start": v(-687.18, -343.83) * mm, "end": v(-636.57, -343.83) * mm});
            skLineSegment(sketch, "E753", {"start": v(-687.18, -353.99) * mm, "end": v(-687.18, -343.83) * mm});
            skLineSegment(sketch, "E754", {"start": v(-687.18, -153.84) * mm, "end": v(-636.57, -153.84) * mm});
            skLineSegment(sketch, "E755", {"start": v(-687.18, -143.68) * mm, "end": v(-687.18, -153.84) * mm});
            skArc(sketch, "E756", {"start": v(-623.43, -166.98) * mm, "mid": v(-627.28, -157.69) * mm, "end": v(-636.57, -153.84) * mm});
            skLineSegment(sketch, "E757", {"start": v(-603.93, -343.83) * mm, "end": v(-553.32, -343.83) * mm});
            skLineSegment(sketch, "E758", {"start": v(-553.32, -353.99) * mm, "end": v(-553.32, -343.83) * mm});
            skLineSegment(sketch, "E759", {"start": v(-603.93, -153.84) * mm, "end": v(-553.32, -153.84) * mm});
            skLineSegment(sketch, "E760", {"start": v(-553.32, -143.68) * mm, "end": v(-553.32, -153.84) * mm});
            skLineSegment(sketch, "E761", {"start": v(-632.62, -366.35) * mm, "end": v(-607.9, -341.63) * mm});
            skLineSegment(sketch, "E762", {"start": v(-632.62, -341.63) * mm, "end": v(-607.9, -366.35) * mm});
            skLineSegment(sketch, "E763", {"start": v(-306.07, -353.96) * mm, "end": v(-306.07, -328.56) * mm});
            skLineSegment(sketch, "E764", {"start": v(-439.93, -328.56) * mm, "end": v(-439.93, -353.96) * mm});
            skLineSegment(sketch, "E765", {"start": v(-376.17, -353.96) * mm, "end": v(-376.17, -328.56) * mm});
            skLineSegment(sketch, "E766", {"start": v(-369.82, -353.96) * mm, "end": v(-369.82, -328.56) * mm});
            skLineSegment(sketch, "E767", {"start": v(-439.93, -353.96) * mm, "end": v(-306.07, -353.96) * mm});
            skLineSegment(sketch, "E768", {"start": v(-306.07, -328.56) * mm, "end": v(-439.93, -328.56) * mm});
            skLineSegment(sketch, "E769", {"start": v(-385.36, -366.33) * mm, "end": v(-360.64, -341.6) * mm});
            skLineSegment(sketch, "E770", {"start": v(-385.36, -341.6) * mm, "end": v(-360.64, -366.33) * mm});
            skLineSegment(sketch, "E771", {"start": v(-113.05, -353.99) * mm, "end": v(-113.05, -143.68) * mm});
            skLineSegment(sketch, "E772", {"start": v(-138.45, -143.68) * mm, "end": v(-138.45, -353.99) * mm});
            skLineSegment(sketch, "E773", {"start": v(-138.45, -353.99) * mm, "end": v(-113.05, -353.99) * mm});
            skLineSegment(sketch, "E774", {"start": v(-138.45, -343.83) * mm, "end": v(-113.05, -343.83) * mm});
            skLineSegment(sketch, "E775", {"start": v(-113.05, -143.68) * mm, "end": v(-138.45, -143.68) * mm});
            skLineSegment(sketch, "E776", {"start": v(-138.45, -153.84) * mm, "end": v(-113.05, -153.84) * mm});
            skLineSegment(sketch, "E777", {"start": v(-150.8, -366.35) * mm, "end": v(-126.08, -341.63) * mm});
            skLineSegment(sketch, "E778", {"start": v(-150.8, -341.63) * mm, "end": v(-126.08, -366.35) * mm});
            skLineSegment(sketch, "E779", {"start": v(39.02, -353.99) * mm, "end": v(204, -353.99) * mm});
            skLineSegment(sketch, "E780", {"start": v(39.02, -152.57) * mm, "end": v(204, -152.57) * mm});
            skLineSegment(sketch, "E781", {"start": v(137.2, -343.83) * mm, "end": v(204, -343.83) * mm});
            skLineSegment(sketch, "E782", {"start": v(137.2, -162.73) * mm, "end": v(204, -162.73) * mm});
            skLineSegment(sketch, "E783", {"start": v(118.4, -331.24) * mm, "end": v(118.4, -175.32) * mm});
            skLineSegment(sketch, "E784", {"start": v(124.62, -331.24) * mm, "end": v(124.62, -175.32) * mm});
            skLineSegment(sketch, "E785", {"start": v(39.02, -343.83) * mm, "end": v(105.8, -343.83) * mm});
            skLineSegment(sketch, "E786", {"start": v(39.02, -353.99) * mm, "end": v(39.02, -343.83) * mm});
            skArc(sketch, "E787", {"start": v(105.8, -343.83) * mm, "mid": v(114.7, -340.14) * mm, "end": v(118.4, -331.24) * mm});
            skArc(sketch, "E788", {"start": v(124.62, -331.24) * mm, "mid": v(128.3, -340.14) * mm, "end": v(137.2, -343.83) * mm});
            skLineSegment(sketch, "E789", {"start": v(39.02, -162.73) * mm, "end": v(105.8, -162.73) * mm});
            skLineSegment(sketch, "E790", {"start": v(39.02, -152.57) * mm, "end": v(39.02, -162.73) * mm});
            skArc(sketch, "E791", {"start": v(118.4, -175.32) * mm, "mid": v(114.7, -166.41) * mm, "end": v(105.8, -162.73) * mm});
            skArc(sketch, "E792", {"start": v(137.2, -162.73) * mm, "mid": v(128.3, -166.41) * mm, "end": v(124.62, -175.32) * mm});
            skLineSegment(sketch, "E793", {"start": v(204, -353.99) * mm, "end": v(204, -343.83) * mm});
            skLineSegment(sketch, "E794", {"start": v(204, -152.57) * mm, "end": v(204, -162.73) * mm});
            skLineSegment(sketch, "E795", {"start": v(109.14, -366.35) * mm, "end": v(133.87, -341.63) * mm});
            skLineSegment(sketch, "E796", {"start": v(109.14, -341.63) * mm, "end": v(133.87, -366.35) * mm});
            skLineSegment(sketch, "E797", {"start": v(451.32, -353.96) * mm, "end": v(451.32, -328.56) * mm});
            skLineSegment(sketch, "E798", {"start": v(286.22, -328.56) * mm, "end": v(286.22, -353.96) * mm});
            skLineSegment(sketch, "E799", {"start": v(365.66, -353.96) * mm, "end": v(365.66, -328.56) * mm});
            skLineSegment(sketch, "E800", {"start": v(371.89, -353.96) * mm, "end": v(371.89, -328.56) * mm});
            skLineSegment(sketch, "E801", {"start": v(286.22, -353.96) * mm, "end": v(451.32, -353.96) * mm});
            skLineSegment(sketch, "E802", {"start": v(451.32, -328.56) * mm, "end": v(286.22, -328.56) * mm});
            skLineSegment(sketch, "E803", {"start": v(356.41, -366.33) * mm, "end": v(381.14, -341.6) * mm});
            skLineSegment(sketch, "E804", {"start": v(356.41, -341.6) * mm, "end": v(381.14, -366.33) * mm});
            skLineSegment(sketch, "E805", {"start": v(628.7, -353.99) * mm, "end": v(628.7, -152.57) * mm});
            skLineSegment(sketch, "E806", {"start": v(603.3, -152.57) * mm, "end": v(603.3, -353.99) * mm});
            skLineSegment(sketch, "E807", {"start": v(603.3, -353.99) * mm, "end": v(628.7, -353.99) * mm});
            skLineSegment(sketch, "E808", {"start": v(603.3, -343.83) * mm, "end": v(628.7, -343.83) * mm});
            skLineSegment(sketch, "E809", {"start": v(628.7, -152.57) * mm, "end": v(603.3, -152.57) * mm});
            skLineSegment(sketch, "E810", {"start": v(603.3, -162.73) * mm, "end": v(628.7, -162.73) * mm});
            skLineSegment(sketch, "E811", {"start": v(590.94, -366.35) * mm, "end": v(615.67, -341.63) * mm});
            skLineSegment(sketch, "E812", {"start": v(590.94, -341.63) * mm, "end": v(615.67, -366.35) * mm});
            skLineSegment(sketch, "E813", {"start": v(780.27, -353.99) * mm, "end": v(946.26, -353.99) * mm});
            skLineSegment(sketch, "E814", {"start": v(780.27, -149.27) * mm, "end": v(946.26, -149.27) * mm});
            skLineSegment(sketch, "E815", {"start": v(879.68, -342.18) * mm, "end": v(946.26, -342.18) * mm});
            skLineSegment(sketch, "E816", {"start": v(879.68, -161.08) * mm, "end": v(946.26, -161.08) * mm});
            skLineSegment(sketch, "E817", {"start": v(859.65, -329.38) * mm, "end": v(859.65, -173.87) * mm});
            skLineSegment(sketch, "E818", {"start": v(866.89, -329.38) * mm, "end": v(866.89, -173.87) * mm});
            skLineSegment(sketch, "E819", {"start": v(780.27, -342.18) * mm, "end": v(846.85, -342.18) * mm});
            skLineSegment(sketch, "E820", {"start": v(780.27, -353.99) * mm, "end": v(780.27, -342.18) * mm});
            skArc(sketch, "E821", {"start": v(846.85, -342.18) * mm, "mid": v(855.9, -338.43) * mm, "end": v(859.65, -329.38) * mm});
            skArc(sketch, "E822", {"start": v(866.89, -329.38) * mm, "mid": v(870.64, -338.43) * mm, "end": v(879.68, -342.18) * mm});
            skLineSegment(sketch, "E823", {"start": v(780.27, -161.08) * mm, "end": v(846.85, -161.08) * mm});
            skLineSegment(sketch, "E824", {"start": v(780.27, -149.27) * mm, "end": v(780.27, -161.08) * mm});
            skArc(sketch, "E825", {"start": v(859.65, -173.87) * mm, "mid": v(855.9, -164.82) * mm, "end": v(846.85, -161.08) * mm});
            skArc(sketch, "E826", {"start": v(879.68, -161.08) * mm, "mid": v(870.64, -164.82) * mm, "end": v(866.89, -173.87) * mm});
            skLineSegment(sketch, "E827", {"start": v(946.26, -353.99) * mm, "end": v(946.26, -342.18) * mm});
            skLineSegment(sketch, "E828", {"start": v(946.26, -149.27) * mm, "end": v(946.26, -161.08) * mm});
            skLineSegment(sketch, "E829", {"start": v(850.9, -366.35) * mm, "end": v(875.63, -341.63) * mm});
            skLineSegment(sketch, "E830", {"start": v(850.9, -341.63) * mm, "end": v(875.63, -366.35) * mm});
            skLineSegment(sketch, "E831", {"start": v(1193.52, -353.96) * mm, "end": v(1193.52, -328.56) * mm});
            skLineSegment(sketch, "E832", {"start": v(1027.53, -328.56) * mm, "end": v(1027.53, -353.96) * mm});
            skLineSegment(sketch, "E833", {"start": v(1106.9, -353.96) * mm, "end": v(1106.9, -328.56) * mm});
            skLineSegment(sketch, "E834", {"start": v(1114.14, -353.96) * mm, "end": v(1114.14, -328.56) * mm});
            skLineSegment(sketch, "E835", {"start": v(1027.53, -353.96) * mm, "end": v(1193.52, -353.96) * mm});
            skLineSegment(sketch, "E836", {"start": v(1193.52, -328.56) * mm, "end": v(1027.53, -328.56) * mm});
            skLineSegment(sketch, "E837", {"start": v(1098.16, -366.33) * mm, "end": v(1122.89, -341.6) * mm});
            skLineSegment(sketch, "E838", {"start": v(1098.16, -341.6) * mm, "end": v(1122.89, -366.33) * mm});
            skLineSegment(sketch, "E839", {"start": v(1345.08, -353.99) * mm, "end": v(1370.48, -353.99) * mm});
            skLineSegment(sketch, "E840", {"start": v(1345.08, -342.18) * mm, "end": v(1370.48, -342.18) * mm});
            skLineSegment(sketch, "E841", {"start": v(1370.48, -149.27) * mm, "end": v(1345.08, -149.27) * mm});
            skLineSegment(sketch, "E842", {"start": v(1345.08, -161.08) * mm, "end": v(1370.48, -161.08) * mm});
            skLineSegment(sketch, "E843", {"start": v(1345.08, -149.27) * mm, "end": v(1345.08, -353.99) * mm});
            skLineSegment(sketch, "E844", {"start": v(1370.48, -353.99) * mm, "end": v(1370.48, -149.27) * mm});
            skLineSegment(sketch, "E845", {"start": v(1332.71, -366.35) * mm, "end": v(1357.44, -341.63) * mm});
            skLineSegment(sketch, "E846", {"start": v(1332.71, -341.63) * mm, "end": v(1357.44, -366.35) * mm});
            skLineSegment(sketch, "E847", {"start": v(-1463.55, -724.3) * mm, "end": v(-1260.48, -724.3) * mm});
            skLineSegment(sketch, "E848", {"start": v(-1463.55, -521.1) * mm, "end": v(-1260.48, -521.1) * mm});
            skLineSegment(sketch, "E849", {"start": v(-1345.7, -713.26) * mm, "end": v(-1260.48, -713.26) * mm});
            skLineSegment(sketch, "E850", {"start": v(-1345.7, -532.16) * mm, "end": v(-1260.48, -532.16) * mm});
            skLineSegment(sketch, "E851", {"start": v(-1365.63, -700.56) * mm, "end": v(-1365.63, -544.86) * mm});
            skLineSegment(sketch, "E852", {"start": v(-1358.4, -700.56) * mm, "end": v(-1358.4, -544.86) * mm});
            skLineSegment(sketch, "E853", {"start": v(-1463.55, -713.26) * mm, "end": v(-1378.33, -713.26) * mm});
            skLineSegment(sketch, "E854", {"start": v(-1463.55, -724.3) * mm, "end": v(-1463.55, -713.26) * mm});
            skArc(sketch, "E855", {"start": v(-1378.33, -713.26) * mm, "mid": v(-1369.35, -709.54) * mm, "end": v(-1365.63, -700.56) * mm});
            skArc(sketch, "E856", {"start": v(-1358.4, -700.56) * mm, "mid": v(-1354.68, -709.54) * mm, "end": v(-1345.7, -713.26) * mm});
            skLineSegment(sketch, "E857", {"start": v(-1463.55, -532.16) * mm, "end": v(-1378.33, -532.16) * mm});
            skLineSegment(sketch, "E858", {"start": v(-1463.55, -521.1) * mm, "end": v(-1463.55, -532.16) * mm});
            skArc(sketch, "E859", {"start": v(-1365.63, -544.86) * mm, "mid": v(-1369.35, -535.88) * mm, "end": v(-1378.33, -532.16) * mm});
            skArc(sketch, "E860", {"start": v(-1345.7, -532.16) * mm, "mid": v(-1354.68, -535.88) * mm, "end": v(-1358.4, -544.86) * mm});
            skLineSegment(sketch, "E861", {"start": v(-1260.48, -724.3) * mm, "end": v(-1260.48, -713.26) * mm});
            skLineSegment(sketch, "E862", {"start": v(-1260.48, -521.1) * mm, "end": v(-1260.48, -532.16) * mm});
            skLineSegment(sketch, "E863", {"start": v(-1374.38, -736.67) * mm, "end": v(-1349.65, -711.95) * mm});
            skLineSegment(sketch, "E864", {"start": v(-1374.38, -711.95) * mm, "end": v(-1349.65, -736.67) * mm});
            skLineSegment(sketch, "E865", {"start": v(-1013.24, -724.33) * mm, "end": v(-1013.24, -698.93) * mm});
            skLineSegment(sketch, "E866", {"start": v(-1216.31, -698.93) * mm, "end": v(-1216.31, -724.33) * mm});
            skLineSegment(sketch, "E867", {"start": v(-1118.4, -724.33) * mm, "end": v(-1118.4, -698.93) * mm});
            skLineSegment(sketch, "E868", {"start": v(-1111.15, -724.33) * mm, "end": v(-1111.15, -698.93) * mm});
            skLineSegment(sketch, "E869", {"start": v(-1216.31, -724.33) * mm, "end": v(-1013.24, -724.33) * mm});
            skLineSegment(sketch, "E870", {"start": v(-1013.24, -698.93) * mm, "end": v(-1216.31, -698.93) * mm});
            skLineSegment(sketch, "E871", {"start": v(-1127.14, -736.7) * mm, "end": v(-1102.41, -711.97) * mm});
            skLineSegment(sketch, "E872", {"start": v(-1127.14, -711.97) * mm, "end": v(-1102.41, -736.7) * mm});
            skLineSegment(sketch, "E873", {"start": v(-854.82, -521.13) * mm, "end": v(-880.22, -521.13) * mm});
            skLineSegment(sketch, "E874", {"start": v(-880.22, -532.18) * mm, "end": v(-854.82, -532.18) * mm});
            skLineSegment(sketch, "E875", {"start": v(-880.22, -724.33) * mm, "end": v(-854.82, -724.33) * mm});
            skLineSegment(sketch, "E876", {"start": v(-880.22, -713.28) * mm, "end": v(-854.82, -713.28) * mm});
            skLineSegment(sketch, "E877", {"start": v(-880.22, -521.13) * mm, "end": v(-880.22, -724.33) * mm});
            skLineSegment(sketch, "E878", {"start": v(-854.82, -724.33) * mm, "end": v(-854.82, -521.13) * mm});
            skLineSegment(sketch, "E879", {"start": v(-892.58, -736.7) * mm, "end": v(-867.86, -711.97) * mm});
            skLineSegment(sketch, "E880", {"start": v(-892.58, -711.97) * mm, "end": v(-867.86, -736.7) * mm});
            skLineSegment(sketch, "E881", {"start": v(-722.1, -724.3) * mm, "end": v(-518.39, -724.3) * mm});
            skLineSegment(sketch, "E882", {"start": v(-722.1, -518.06) * mm, "end": v(-518.39, -518.06) * mm});
            skArc(sketch, "E883", {"start": v(-616.3, -698.84) * mm, "mid": v(-612.53, -707.96) * mm, "end": v(-603.41, -711.74) * mm});
            skArc(sketch, "E884", {"start": v(-603.41, -530.63) * mm, "mid": v(-612.53, -534.4) * mm, "end": v(-616.3, -543.52) * mm});
            skLineSegment(sketch, "E885", {"start": v(-624.18, -698.84) * mm, "end": v(-624.18, -543.52) * mm});
            skLineSegment(sketch, "E886", {"start": v(-616.3, -698.84) * mm, "end": v(-616.3, -543.52) * mm});
            skLineSegment(sketch, "E887", {"start": v(-722.1, -711.74) * mm, "end": v(-637.07, -711.74) * mm});
            skLineSegment(sketch, "E888", {"start": v(-722.1, -724.3) * mm, "end": v(-722.1, -711.74) * mm});
            skArc(sketch, "E889", {"start": v(-637.07, -711.74) * mm, "mid": v(-627.95, -707.96) * mm, "end": v(-624.18, -698.84) * mm});
            skLineSegment(sketch, "E890", {"start": v(-722.1, -530.63) * mm, "end": v(-637.07, -530.63) * mm});
            skLineSegment(sketch, "E891", {"start": v(-722.1, -518.06) * mm, "end": v(-722.1, -530.63) * mm});
            skArc(sketch, "E892", {"start": v(-624.18, -543.52) * mm, "mid": v(-627.95, -534.4) * mm, "end": v(-637.07, -530.63) * mm});
            skLineSegment(sketch, "E893", {"start": v(-603.41, -711.74) * mm, "end": v(-518.39, -711.74) * mm});
            skLineSegment(sketch, "E894", {"start": v(-518.39, -724.3) * mm, "end": v(-518.39, -711.74) * mm});
            skLineSegment(sketch, "E895", {"start": v(-603.41, -530.63) * mm, "end": v(-518.39, -530.63) * mm});
            skLineSegment(sketch, "E896", {"start": v(-518.39, -518.06) * mm, "end": v(-518.39, -530.63) * mm});
            skLineSegment(sketch, "E897", {"start": v(-632.6, -736.67) * mm, "end": v(-607.88, -711.95) * mm});
            skLineSegment(sketch, "E898", {"start": v(-632.6, -711.95) * mm, "end": v(-607.88, -736.67) * mm});
            skLineSegment(sketch, "E899", {"start": v(-271.46, -724.33) * mm, "end": v(-271.46, -698.93) * mm});
            skLineSegment(sketch, "E900", {"start": v(-474.54, -698.93) * mm, "end": v(-474.54, -724.33) * mm});
            skLineSegment(sketch, "E901", {"start": v(-376.62, -724.33) * mm, "end": v(-376.62, -698.93) * mm});
            skLineSegment(sketch, "E902", {"start": v(-369.38, -724.33) * mm, "end": v(-369.38, -698.93) * mm});
            skLineSegment(sketch, "E903", {"start": v(-474.54, -724.33) * mm, "end": v(-271.46, -724.33) * mm});
            skLineSegment(sketch, "E904", {"start": v(-271.46, -698.93) * mm, "end": v(-474.54, -698.93) * mm});
            skLineSegment(sketch, "E905", {"start": v(-385.36, -736.7) * mm, "end": v(-360.64, -711.97) * mm});
            skLineSegment(sketch, "E906", {"start": v(-385.36, -711.97) * mm, "end": v(-360.64, -736.7) * mm});
            skLineSegment(sketch, "E907", {"start": v(-113.05, -518.06) * mm, "end": v(-138.45, -518.06) * mm});
            skLineSegment(sketch, "E908", {"start": v(-138.45, -530.63) * mm, "end": v(-113.05, -530.63) * mm});
            skLineSegment(sketch, "E909", {"start": v(-138.45, -724.3) * mm, "end": v(-113.05, -724.3) * mm});
            skLineSegment(sketch, "E910", {"start": v(-138.45, -711.74) * mm, "end": v(-113.05, -711.74) * mm});
            skLineSegment(sketch, "E911", {"start": v(-138.45, -518.06) * mm, "end": v(-138.45, -724.3) * mm});
            skLineSegment(sketch, "E912", {"start": v(-113.05, -724.3) * mm, "end": v(-113.05, -518.06) * mm});
            skLineSegment(sketch, "E913", {"start": v(-150.8, -736.67) * mm, "end": v(-126.08, -711.95) * mm});
            skLineSegment(sketch, "E914", {"start": v(-150.8, -711.95) * mm, "end": v(-126.08, -736.67) * mm});
            skLineSegment(sketch, "E915", {"start": v(19.02, -724.33) * mm, "end": v(224, -724.33) * mm});
            skLineSegment(sketch, "E916", {"start": v(19.02, -514.78) * mm, "end": v(224, -514.78) * mm});
            skLineSegment(sketch, "E917", {"start": v(139.18, -710.1) * mm, "end": v(224, -710.1) * mm});
            skLineSegment(sketch, "E918", {"start": v(139.18, -529) * mm, "end": v(224, -529) * mm});
            skLineSegment(sketch, "E919", {"start": v(116.94, -697.01) * mm, "end": v(116.94, -542.1) * mm});
            skLineSegment(sketch, "E920", {"start": v(126.08, -697.01) * mm, "end": v(126.08, -542.1) * mm});
            skLineSegment(sketch, "E921", {"start": v(19.02, -710.1) * mm, "end": v(103.84, -710.1) * mm});
            skLineSegment(sketch, "E922", {"start": v(19.02, -724.33) * mm, "end": v(19.02, -710.1) * mm});
            skArc(sketch, "E923", {"start": v(103.84, -710.1) * mm, "mid": v(113.1, -706.27) * mm, "end": v(116.94, -697.01) * mm});
            skArc(sketch, "E924", {"start": v(126.08, -697.01) * mm, "mid": v(129.92, -706.27) * mm, "end": v(139.18, -710.1) * mm});
            skLineSegment(sketch, "E925", {"start": v(19.02, -529) * mm, "end": v(103.84, -529) * mm});
            skLineSegment(sketch, "E926", {"start": v(19.02, -514.78) * mm, "end": v(19.02, -529) * mm});
            skArc(sketch, "E927", {"start": v(116.94, -542.1) * mm, "mid": v(113.1, -532.84) * mm, "end": v(103.84, -529) * mm});
            skArc(sketch, "E928", {"start": v(139.18, -529) * mm, "mid": v(129.92, -532.84) * mm, "end": v(126.08, -542.1) * mm});
            skLineSegment(sketch, "E929", {"start": v(224, -724.33) * mm, "end": v(224, -710.1) * mm});
            skLineSegment(sketch, "E930", {"start": v(224, -514.78) * mm, "end": v(224, -529) * mm});
            skLineSegment(sketch, "E931", {"start": v(109.14, -736.7) * mm, "end": v(133.87, -711.97) * mm});
            skLineSegment(sketch, "E932", {"start": v(109.14, -711.97) * mm, "end": v(133.87, -736.7) * mm});
            skLineSegment(sketch, "E933", {"start": v(470.62, -698.93) * mm, "end": v(266.9, -698.93) * mm});
            skLineSegment(sketch, "E934", {"start": v(266.9, -724.33) * mm, "end": v(470.62, -724.33) * mm});
            skLineSegment(sketch, "E935", {"start": v(266.9, -698.93) * mm, "end": v(266.9, -724.33) * mm});
            skLineSegment(sketch, "E936", {"start": v(470.62, -724.33) * mm, "end": v(470.62, -698.93) * mm});
            skLineSegment(sketch, "E937", {"start": v(364.19, -724.33) * mm, "end": v(364.19, -698.93) * mm});
            skLineSegment(sketch, "E938", {"start": v(373.33, -724.33) * mm, "end": v(373.33, -698.93) * mm});
            skLineSegment(sketch, "E939", {"start": v(356.4, -736.7) * mm, "end": v(381.12, -711.97) * mm});
            skLineSegment(sketch, "E940", {"start": v(356.4, -711.97) * mm, "end": v(381.12, -736.7) * mm});
            skLineSegment(sketch, "E941", {"start": v(628.72, -514.76) * mm, "end": v(603.32, -514.76) * mm});
            skLineSegment(sketch, "E942", {"start": v(603.32, -528.98) * mm, "end": v(628.72, -528.98) * mm});
            skLineSegment(sketch, "E943", {"start": v(603.32, -724.3) * mm, "end": v(628.72, -724.3) * mm});
            skLineSegment(sketch, "E944", {"start": v(603.32, -710.08) * mm, "end": v(628.72, -710.08) * mm});
            skLineSegment(sketch, "E945", {"start": v(603.32, -514.76) * mm, "end": v(603.32, -724.3) * mm});
            skLineSegment(sketch, "E946", {"start": v(628.72, -724.3) * mm, "end": v(628.72, -514.76) * mm});
            skLineSegment(sketch, "E947", {"start": v(590.95, -736.67) * mm, "end": v(615.68, -711.95) * mm});
            skLineSegment(sketch, "E948", {"start": v(590.95, -711.95) * mm, "end": v(615.68, -736.67) * mm});
            skLineSegment(sketch, "E949", {"start": v(760.26, -724.33) * mm, "end": v(966.25, -724.33) * mm});
            skLineSegment(sketch, "E950", {"start": v(760.26, -508.43) * mm, "end": v(966.25, -508.43) * mm});
            skLineSegment(sketch, "E951", {"start": v(881.83, -706.93) * mm, "end": v(966.25, -706.93) * mm});
            skLineSegment(sketch, "E952", {"start": v(881.83, -525.83) * mm, "end": v(966.25, -525.83) * mm});
            skLineSegment(sketch, "E953", {"start": v(858.18, -693.44) * mm, "end": v(858.18, -539.33) * mm});
            skLineSegment(sketch, "E954", {"start": v(868.34, -693.44) * mm, "end": v(868.34, -539.33) * mm});
            skLineSegment(sketch, "E955", {"start": v(760.26, -706.93) * mm, "end": v(844.68, -706.93) * mm});
            skLineSegment(sketch, "E956", {"start": v(760.26, -724.33) * mm, "end": v(760.26, -706.93) * mm});
            skArc(sketch, "E957", {"start": v(844.68, -706.93) * mm, "mid": v(854.22, -702.98) * mm, "end": v(858.18, -693.44) * mm});
            skArc(sketch, "E958", {"start": v(868.34, -693.44) * mm, "mid": v(872.29, -702.98) * mm, "end": v(881.83, -706.93) * mm});
            skLineSegment(sketch, "E959", {"start": v(760.26, -525.83) * mm, "end": v(844.68, -525.83) * mm});
            skLineSegment(sketch, "E960", {"start": v(760.26, -508.43) * mm, "end": v(760.26, -525.83) * mm});
            skArc(sketch, "E961", {"start": v(858.18, -539.33) * mm, "mid": v(854.22, -529.78) * mm, "end": v(844.68, -525.83) * mm});
            skArc(sketch, "E962", {"start": v(881.83, -525.83) * mm, "mid": v(872.29, -529.78) * mm, "end": v(868.34, -539.33) * mm});
            skLineSegment(sketch, "E963", {"start": v(966.25, -724.33) * mm, "end": v(966.25, -706.93) * mm});
            skLineSegment(sketch, "E964", {"start": v(966.25, -508.43) * mm, "end": v(966.25, -525.83) * mm});
            skLineSegment(sketch, "E965", {"start": v(850.9, -736.7) * mm, "end": v(875.62, -711.97) * mm});
            skLineSegment(sketch, "E966", {"start": v(850.9, -711.97) * mm, "end": v(875.62, -736.7) * mm});
            skLineSegment(sketch, "E967", {"start": v(1213.52, -724.3) * mm, "end": v(1213.52, -698.9) * mm});
            skLineSegment(sketch, "E968", {"start": v(1007.53, -698.9) * mm, "end": v(1007.53, -724.3) * mm});
            skLineSegment(sketch, "E969", {"start": v(1105.44, -724.3) * mm, "end": v(1105.44, -698.9) * mm});
            skLineSegment(sketch, "E970", {"start": v(1115.6, -724.3) * mm, "end": v(1115.6, -698.9) * mm});
            skLineSegment(sketch, "E971", {"start": v(1007.53, -724.3) * mm, "end": v(1213.52, -724.3) * mm});
            skLineSegment(sketch, "E972", {"start": v(1213.52, -698.9) * mm, "end": v(1007.53, -698.9) * mm});
            skLineSegment(sketch, "E973", {"start": v(1098.16, -736.67) * mm, "end": v(1122.89, -711.95) * mm});
            skLineSegment(sketch, "E974", {"start": v(1098.16, -711.95) * mm, "end": v(1122.89, -736.67) * mm});
            skLineSegment(sketch, "E975", {"start": v(1345.08, -724.33) * mm, "end": v(1370.48, -724.33) * mm});
            skLineSegment(sketch, "E976", {"start": v(1345.08, -706.93) * mm, "end": v(1370.48, -706.93) * mm});
            skLineSegment(sketch, "E977", {"start": v(1370.48, -508.43) * mm, "end": v(1345.08, -508.43) * mm});
            skLineSegment(sketch, "E978", {"start": v(1345.08, -525.83) * mm, "end": v(1370.48, -525.83) * mm});
            skLineSegment(sketch, "E979", {"start": v(1345.08, -508.43) * mm, "end": v(1345.08, -724.33) * mm});
            skLineSegment(sketch, "E980", {"start": v(1370.48, -724.33) * mm, "end": v(1370.48, -508.43) * mm});
            skLineSegment(sketch, "E981", {"start": v(1332.71, -736.7) * mm, "end": v(1357.44, -711.97) * mm});
            skLineSegment(sketch, "E982", {"start": v(1332.71, -711.97) * mm, "end": v(1357.44, -736.7) * mm});
            skSolve(sketch);
        }
        {
            var Q0;
            Q0 = qSketchRegion(id + "F3", true);
            extrude(context, id + "F4", {"entities" : qUnion([Q0]), "depth" : 304.8 * mm});
        }
        {
            var Q0;
            Q0=makeQuery(id+"F4.opExtrude","SWEPT_BODY",BODY,{"disambiguationData":[OSD([sQuery(id+"F3.wireOp",EDGE,"E423"),sQuery(id+"F3.wireOp",EDGE,"E424"),sQuery(id+"F3.wireOp",EDGE,"E427"),sQuery(id+"F3.wireOp",EDGE,"E428")])]});
            var Q1;
            Q1=makeQuery(id+"F4.opExtrude","SWEPT_BODY",BODY,{"disambiguationData":[OSD([sQuery(id+"F3.wireOp",EDGE,"E432"),sQuery(id+"F3.wireOp",EDGE,"E434"),sQuery(id+"F3.wireOp",EDGE,"E435"),sQuery(id+"F3.wireOp",EDGE,"E436")])]});
            var Q2;
            Q2=makeQuery(id+"F4.opExtrude","SWEPT_BODY",BODY,{"disambiguationData":[OSD([sQuery(id+"F3.wireOp",EDGE,"E439"),sQuery(id+"F3.wireOp",EDGE,"E440"),sQuery(id+"F3.wireOp",EDGE,"E441"),sQuery(id+"F3.wireOp",EDGE,"E442"),sQuery(id+"F3.wireOp",EDGE,"E443"),sQuery(id+"F3.wireOp",EDGE,"E444"),sQuery(id+"F3.wireOp",EDGE,"E445"),sQuery(id+"F3.wireOp",EDGE,"E446"),sQuery(id+"F3.wireOp",EDGE,"E447"),sQuery(id+"F3.wireOp",EDGE,"E448"),sQuery(id+"F3.wireOp",EDGE,"E449"),sQuery(id+"F3.wireOp",EDGE,"E450"),sQuery(id+"F3.wireOp",EDGE,"E451"),sQuery(id+"F3.wireOp",EDGE,"E452"),sQuery(id+"F3.wireOp",EDGE,"E453"),sQuery(id+"F3.wireOp",EDGE,"E454")])]});
            var Q3;
            Q3=makeQuery(id+"F4.opExtrude","SWEPT_BODY",BODY,{"disambiguationData":[OSD([sQuery(id+"F3.wireOp",EDGE,"E457"),sQuery(id+"F3.wireOp",EDGE,"E458"),sQuery(id+"F3.wireOp",EDGE,"E461"),sQuery(id+"F3.wireOp",EDGE,"E462")])]});
            var Q4;
            Q4=makeQuery(id+"F4.opExtrude","SWEPT_BODY",BODY,{"disambiguationData":[OSD([sQuery(id+"F3.wireOp",EDGE,"E466"),sQuery(id+"F3.wireOp",EDGE,"E468"),sQuery(id+"F3.wireOp",EDGE,"E469"),sQuery(id+"F3.wireOp",EDGE,"E470")])]});
            var Q5;
            Q5=makeQuery(id+"F4.opExtrude","SWEPT_BODY",BODY,{"disambiguationData":[OSD([sQuery(id+"F3.wireOp",EDGE,"E473"),sQuery(id+"F3.wireOp",EDGE,"E474"),sQuery(id+"F3.wireOp",EDGE,"E475"),sQuery(id+"F3.wireOp",EDGE,"E476"),sQuery(id+"F3.wireOp",EDGE,"E477"),sQuery(id+"F3.wireOp",EDGE,"E478"),sQuery(id+"F3.wireOp",EDGE,"E479"),sQuery(id+"F3.wireOp",EDGE,"E480"),sQuery(id+"F3.wireOp",EDGE,"E481"),sQuery(id+"F3.wireOp",EDGE,"E482"),sQuery(id+"F3.wireOp",EDGE,"E483"),sQuery(id+"F3.wireOp",EDGE,"E484"),sQuery(id+"F3.wireOp",EDGE,"E485"),sQuery(id+"F3.wireOp",EDGE,"E486"),sQuery(id+"F3.wireOp",EDGE,"E487"),sQuery(id+"F3.wireOp",EDGE,"E488")])]});
            var Q6;
            Q6=makeQuery(id+"F4.opExtrude","SWEPT_BODY",BODY,{"disambiguationData":[OSD([sQuery(id+"F3.wireOp",EDGE,"E491"),sQuery(id+"F3.wireOp",EDGE,"E492"),sQuery(id+"F3.wireOp",EDGE,"E495"),sQuery(id+"F3.wireOp",EDGE,"E496")])]});
            var Q7;
            Q7=makeQuery(id+"F4.opExtrude","SWEPT_BODY",BODY,{"disambiguationData":[OSD([sQuery(id+"F3.wireOp",EDGE,"E499"),sQuery(id+"F3.wireOp",EDGE,"E501"),sQuery(id+"F3.wireOp",EDGE,"E503"),sQuery(id+"F3.wireOp",EDGE,"E504")])]});
            var Q8;
            Q8=makeQuery(id+"F4.opExtrude","SWEPT_BODY",BODY,{"disambiguationData":[OSD([sQuery(id+"F3.wireOp",EDGE,"E507"),sQuery(id+"F3.wireOp",EDGE,"E508"),sQuery(id+"F3.wireOp",EDGE,"E509"),sQuery(id+"F3.wireOp",EDGE,"E510"),sQuery(id+"F3.wireOp",EDGE,"E511"),sQuery(id+"F3.wireOp",EDGE,"E512"),sQuery(id+"F3.wireOp",EDGE,"E513"),sQuery(id+"F3.wireOp",EDGE,"E514"),sQuery(id+"F3.wireOp",EDGE,"E515"),sQuery(id+"F3.wireOp",EDGE,"E516"),sQuery(id+"F3.wireOp",EDGE,"E517"),sQuery(id+"F3.wireOp",EDGE,"E518"),sQuery(id+"F3.wireOp",EDGE,"E519"),sQuery(id+"F3.wireOp",EDGE,"E520"),sQuery(id+"F3.wireOp",EDGE,"E521"),sQuery(id+"F3.wireOp",EDGE,"E522")])]});
            var Q9;
            Q9=makeQuery(id+"F4.opExtrude","SWEPT_BODY",BODY,{"disambiguationData":[OSD([sQuery(id+"F3.wireOp",EDGE,"E525"),sQuery(id+"F3.wireOp",EDGE,"E528"),sQuery(id+"F3.wireOp",EDGE,"E529"),sQuery(id+"F3.wireOp",EDGE,"E530")])]});
            var Q10;
            Q10=makeQuery(id+"F4.opExtrude","SWEPT_BODY",BODY,{"disambiguationData":[OSD([sQuery(id+"F3.wireOp",EDGE,"E533"),sQuery(id+"F3.wireOp",EDGE,"E536"),sQuery(id+"F3.wireOp",EDGE,"E537"),sQuery(id+"F3.wireOp",EDGE,"E538")])]});
            var Q11;
            Q11=makeQuery(id+"F4.opExtrude","SWEPT_BODY",BODY,{"disambiguationData":[OSD([sQuery(id+"F3.wireOp",EDGE,"E541"),sQuery(id+"F3.wireOp",EDGE,"E542"),sQuery(id+"F3.wireOp",EDGE,"E543"),sQuery(id+"F3.wireOp",EDGE,"E544"),sQuery(id+"F3.wireOp",EDGE,"E545"),sQuery(id+"F3.wireOp",EDGE,"E546"),sQuery(id+"F3.wireOp",EDGE,"E547"),sQuery(id+"F3.wireOp",EDGE,"E548"),sQuery(id+"F3.wireOp",EDGE,"E549"),sQuery(id+"F3.wireOp",EDGE,"E550"),sQuery(id+"F3.wireOp",EDGE,"E551"),sQuery(id+"F3.wireOp",EDGE,"E552"),sQuery(id+"F3.wireOp",EDGE,"E553"),sQuery(id+"F3.wireOp",EDGE,"E554"),sQuery(id+"F3.wireOp",EDGE,"E555"),sQuery(id+"F3.wireOp",EDGE,"E556")])]});
            var Q12;
            Q12=makeQuery(id+"F4.opExtrude","SWEPT_BODY",BODY,{"disambiguationData":[OSD([sQuery(id+"F3.wireOp",EDGE,"E559"),sQuery(id+"F3.wireOp",EDGE,"E560"),sQuery(id+"F3.wireOp",EDGE,"E561"),sQuery(id+"F3.wireOp",EDGE,"E562")])]});
            var Q13;
            Q13=makeQuery(id+"F4.opExtrude","SWEPT_BODY",BODY,{"disambiguationData":[OSD([sQuery(id+"F3.wireOp",EDGE,"E567"),sQuery(id+"F3.wireOp",EDGE,"E568"),sQuery(id+"F3.wireOp",EDGE,"E570"),sQuery(id+"F3.wireOp",EDGE,"E572")])]});
            var Q14;
            Q14=makeQuery(id+"F4.opExtrude","SWEPT_BODY",BODY,{"disambiguationData":[OSD([sQuery(id+"F3.wireOp",EDGE,"E575"),sQuery(id+"F3.wireOp",EDGE,"E576"),sQuery(id+"F3.wireOp",EDGE,"E577"),sQuery(id+"F3.wireOp",EDGE,"E578"),sQuery(id+"F3.wireOp",EDGE,"E579"),sQuery(id+"F3.wireOp",EDGE,"E580"),sQuery(id+"F3.wireOp",EDGE,"E581"),sQuery(id+"F3.wireOp",EDGE,"E582"),sQuery(id+"F3.wireOp",EDGE,"E583"),sQuery(id+"F3.wireOp",EDGE,"E584"),sQuery(id+"F3.wireOp",EDGE,"E585"),sQuery(id+"F3.wireOp",EDGE,"E586"),sQuery(id+"F3.wireOp",EDGE,"E587"),sQuery(id+"F3.wireOp",EDGE,"E588"),sQuery(id+"F3.wireOp",EDGE,"E589"),sQuery(id+"F3.wireOp",EDGE,"E590")])]});
            var Q15;
            Q15=makeQuery(id+"F4.opExtrude","SWEPT_BODY",BODY,{"disambiguationData":[OSD([sQuery(id+"F3.wireOp",EDGE,"E593"),sQuery(id+"F3.wireOp",EDGE,"E594"),sQuery(id+"F3.wireOp",EDGE,"E595"),sQuery(id+"F3.wireOp",EDGE,"E596")])]});
            var Q16;
            Q16=makeQuery(id+"F4.opExtrude","SWEPT_BODY",BODY,{"disambiguationData":[OSD([sQuery(id+"F3.wireOp",EDGE,"E602"),sQuery(id+"F3.wireOp",EDGE,"E604"),sQuery(id+"F3.wireOp",EDGE,"E605"),sQuery(id+"F3.wireOp",EDGE,"E606")])]});
            var Q17;
            Q17=makeQuery(id+"F4.opExtrude","SWEPT_BODY",BODY,{"disambiguationData":[OSD([sQuery(id+"F3.wireOp",EDGE,"E627"),sQuery(id+"F3.wireOp",EDGE,"E628"),sQuery(id+"F3.wireOp",EDGE,"E631"),sQuery(id+"F3.wireOp",EDGE,"E632")])]});
            var Q18;
            Q18=makeQuery(id+"F4.opExtrude","SWEPT_BODY",BODY,{"disambiguationData":[OSD([sQuery(id+"F3.wireOp",EDGE,"E635"),sQuery(id+"F3.wireOp",EDGE,"E636"),sQuery(id+"F3.wireOp",EDGE,"E637"),sQuery(id+"F3.wireOp",EDGE,"E639")])]});
            var Q19;
            Q19=makeQuery(id+"F4.opExtrude","SWEPT_BODY",BODY,{"disambiguationData":[OSD([sQuery(id+"F3.wireOp",EDGE,"E643"),sQuery(id+"F3.wireOp",EDGE,"E644"),sQuery(id+"F3.wireOp",EDGE,"E645"),sQuery(id+"F3.wireOp",EDGE,"E646"),sQuery(id+"F3.wireOp",EDGE,"E647"),sQuery(id+"F3.wireOp",EDGE,"E648"),sQuery(id+"F3.wireOp",EDGE,"E649"),sQuery(id+"F3.wireOp",EDGE,"E650"),sQuery(id+"F3.wireOp",EDGE,"E651"),sQuery(id+"F3.wireOp",EDGE,"E652"),sQuery(id+"F3.wireOp",EDGE,"E653"),sQuery(id+"F3.wireOp",EDGE,"E654"),sQuery(id+"F3.wireOp",EDGE,"E655"),sQuery(id+"F3.wireOp",EDGE,"E656"),sQuery(id+"F3.wireOp",EDGE,"E657"),sQuery(id+"F3.wireOp",EDGE,"E658")])]});
            var Q20;
            Q20=makeQuery(id+"F4.opExtrude","SWEPT_BODY",BODY,{"disambiguationData":[OSD([sQuery(id+"F3.wireOp",EDGE,"E661"),sQuery(id+"F3.wireOp",EDGE,"E664"),sQuery(id+"F3.wireOp",EDGE,"E665"),sQuery(id+"F3.wireOp",EDGE,"E666")])]});
            var Q21;
            Q21=makeQuery(id+"F4.opExtrude","SWEPT_BODY",BODY,{"disambiguationData":[OSD([sQuery(id+"F3.wireOp",EDGE,"E669"),sQuery(id+"F3.wireOp",EDGE,"E670"),sQuery(id+"F3.wireOp",EDGE,"E671"),sQuery(id+"F3.wireOp",EDGE,"E673")])]});
            var Q22;
            Q22=makeQuery(id+"F4.opExtrude","SWEPT_BODY",BODY,{"disambiguationData":[OSD([sQuery(id+"F3.wireOp",EDGE,"E695"),sQuery(id+"F3.wireOp",EDGE,"E696"),sQuery(id+"F3.wireOp",EDGE,"E699"),sQuery(id+"F3.wireOp",EDGE,"E700")])]});
            var Q23;
            Q23=makeQuery(id+"F4.opExtrude","SWEPT_BODY",BODY,{"disambiguationData":[OSD([sQuery(id+"F3.wireOp",EDGE,"E703"),sQuery(id+"F3.wireOp",EDGE,"E705"),sQuery(id+"F3.wireOp",EDGE,"E707"),sQuery(id+"F3.wireOp",EDGE,"E708")])]});
            var Q24;
            Q24=makeQuery(id+"F4.opExtrude","SWEPT_BODY",BODY,{"disambiguationData":[OSD([sQuery(id+"F3.wireOp",EDGE,"E711"),sQuery(id+"F3.wireOp",EDGE,"E712"),sQuery(id+"F3.wireOp",EDGE,"E713"),sQuery(id+"F3.wireOp",EDGE,"E714"),sQuery(id+"F3.wireOp",EDGE,"E715"),sQuery(id+"F3.wireOp",EDGE,"E716"),sQuery(id+"F3.wireOp",EDGE,"E717"),sQuery(id+"F3.wireOp",EDGE,"E718"),sQuery(id+"F3.wireOp",EDGE,"E719"),sQuery(id+"F3.wireOp",EDGE,"E720"),sQuery(id+"F3.wireOp",EDGE,"E721"),sQuery(id+"F3.wireOp",EDGE,"E722"),sQuery(id+"F3.wireOp",EDGE,"E723"),sQuery(id+"F3.wireOp",EDGE,"E724"),sQuery(id+"F3.wireOp",EDGE,"E725"),sQuery(id+"F3.wireOp",EDGE,"E726")])]});
            var Q25;
            Q25=makeQuery(id+"F4.opExtrude","SWEPT_BODY",BODY,{"disambiguationData":[OSD([sQuery(id+"F3.wireOp",EDGE,"E729"),sQuery(id+"F3.wireOp",EDGE,"E730"),sQuery(id+"F3.wireOp",EDGE,"E733"),sQuery(id+"F3.wireOp",EDGE,"E734")])]});
            var Q26;
            Q26=makeQuery(id+"F4.opExtrude","SWEPT_BODY",BODY,{"disambiguationData":[OSD([sQuery(id+"F3.wireOp",EDGE,"E737"),sQuery(id+"F3.wireOp",EDGE,"E739"),sQuery(id+"F3.wireOp",EDGE,"E741"),sQuery(id+"F3.wireOp",EDGE,"E742")])]});
            var Q27;
            Q27=makeQuery(id+"F4.opExtrude","SWEPT_BODY",BODY,{"disambiguationData":[OSD([sQuery(id+"F3.wireOp",EDGE,"E745"),sQuery(id+"F3.wireOp",EDGE,"E746"),sQuery(id+"F3.wireOp",EDGE,"E747"),sQuery(id+"F3.wireOp",EDGE,"E748"),sQuery(id+"F3.wireOp",EDGE,"E749"),sQuery(id+"F3.wireOp",EDGE,"E750"),sQuery(id+"F3.wireOp",EDGE,"E751"),sQuery(id+"F3.wireOp",EDGE,"E752"),sQuery(id+"F3.wireOp",EDGE,"E753"),sQuery(id+"F3.wireOp",EDGE,"E754"),sQuery(id+"F3.wireOp",EDGE,"E755"),sQuery(id+"F3.wireOp",EDGE,"E756"),sQuery(id+"F3.wireOp",EDGE,"E757"),sQuery(id+"F3.wireOp",EDGE,"E758"),sQuery(id+"F3.wireOp",EDGE,"E759"),sQuery(id+"F3.wireOp",EDGE,"E760")])]});
            var Q28;
            Q28=makeQuery(id+"F4.opExtrude","SWEPT_BODY",BODY,{"disambiguationData":[OSD([sQuery(id+"F3.wireOp",EDGE,"E763"),sQuery(id+"F3.wireOp",EDGE,"E764"),sQuery(id+"F3.wireOp",EDGE,"E767"),sQuery(id+"F3.wireOp",EDGE,"E768")])]});
            var Q29;
            Q29=makeQuery(id+"F4.opExtrude","SWEPT_BODY",BODY,{"disambiguationData":[OSD([sQuery(id+"F3.wireOp",EDGE,"E771"),sQuery(id+"F3.wireOp",EDGE,"E772"),sQuery(id+"F3.wireOp",EDGE,"E773"),sQuery(id+"F3.wireOp",EDGE,"E775")])]});
            var Q30;
            Q30=makeQuery(id+"F4.opExtrude","SWEPT_BODY",BODY,{"disambiguationData":[OSD([sQuery(id+"F3.wireOp",EDGE,"E779"),sQuery(id+"F3.wireOp",EDGE,"E780"),sQuery(id+"F3.wireOp",EDGE,"E781"),sQuery(id+"F3.wireOp",EDGE,"E782"),sQuery(id+"F3.wireOp",EDGE,"E783"),sQuery(id+"F3.wireOp",EDGE,"E784"),sQuery(id+"F3.wireOp",EDGE,"E785"),sQuery(id+"F3.wireOp",EDGE,"E786"),sQuery(id+"F3.wireOp",EDGE,"E787"),sQuery(id+"F3.wireOp",EDGE,"E788"),sQuery(id+"F3.wireOp",EDGE,"E789"),sQuery(id+"F3.wireOp",EDGE,"E790"),sQuery(id+"F3.wireOp",EDGE,"E791"),sQuery(id+"F3.wireOp",EDGE,"E792"),sQuery(id+"F3.wireOp",EDGE,"E793"),sQuery(id+"F3.wireOp",EDGE,"E794")])]});
            var Q31;
            Q31=makeQuery(id+"F4.opExtrude","SWEPT_BODY",BODY,{"disambiguationData":[OSD([sQuery(id+"F3.wireOp",EDGE,"E797"),sQuery(id+"F3.wireOp",EDGE,"E798"),sQuery(id+"F3.wireOp",EDGE,"E801"),sQuery(id+"F3.wireOp",EDGE,"E802")])]});
            var Q32;
            Q32=makeQuery(id+"F4.opExtrude","SWEPT_BODY",BODY,{"disambiguationData":[OSD([sQuery(id+"F3.wireOp",EDGE,"E805"),sQuery(id+"F3.wireOp",EDGE,"E806"),sQuery(id+"F3.wireOp",EDGE,"E807"),sQuery(id+"F3.wireOp",EDGE,"E809")])]});
            var Q33;
            Q33=makeQuery(id+"F4.opExtrude","SWEPT_BODY",BODY,{"disambiguationData":[OSD([sQuery(id+"F3.wireOp",EDGE,"E813"),sQuery(id+"F3.wireOp",EDGE,"E814"),sQuery(id+"F3.wireOp",EDGE,"E815"),sQuery(id+"F3.wireOp",EDGE,"E816"),sQuery(id+"F3.wireOp",EDGE,"E817"),sQuery(id+"F3.wireOp",EDGE,"E818"),sQuery(id+"F3.wireOp",EDGE,"E819"),sQuery(id+"F3.wireOp",EDGE,"E820"),sQuery(id+"F3.wireOp",EDGE,"E821"),sQuery(id+"F3.wireOp",EDGE,"E822"),sQuery(id+"F3.wireOp",EDGE,"E823"),sQuery(id+"F3.wireOp",EDGE,"E824"),sQuery(id+"F3.wireOp",EDGE,"E825"),sQuery(id+"F3.wireOp",EDGE,"E826"),sQuery(id+"F3.wireOp",EDGE,"E827"),sQuery(id+"F3.wireOp",EDGE,"E828")])]});
            var Q34;
            Q34=makeQuery(id+"F4.opExtrude","SWEPT_BODY",BODY,{"disambiguationData":[OSD([sQuery(id+"F3.wireOp",EDGE,"E831"),sQuery(id+"F3.wireOp",EDGE,"E832"),sQuery(id+"F3.wireOp",EDGE,"E835"),sQuery(id+"F3.wireOp",EDGE,"E836")])]});
            var Q35;
            Q35=makeQuery(id+"F4.opExtrude","SWEPT_BODY",BODY,{"disambiguationData":[OSD([sQuery(id+"F3.wireOp",EDGE,"E839"),sQuery(id+"F3.wireOp",EDGE,"E841"),sQuery(id+"F3.wireOp",EDGE,"E843"),sQuery(id+"F3.wireOp",EDGE,"E844")])]});
            var Q36;
            Q36=makeQuery(id+"F4.opExtrude","SWEPT_BODY",BODY,{"disambiguationData":[OSD([sQuery(id+"F3.wireOp",EDGE,"E847"),sQuery(id+"F3.wireOp",EDGE,"E848"),sQuery(id+"F3.wireOp",EDGE,"E849"),sQuery(id+"F3.wireOp",EDGE,"E850"),sQuery(id+"F3.wireOp",EDGE,"E851"),sQuery(id+"F3.wireOp",EDGE,"E852"),sQuery(id+"F3.wireOp",EDGE,"E853"),sQuery(id+"F3.wireOp",EDGE,"E854"),sQuery(id+"F3.wireOp",EDGE,"E855"),sQuery(id+"F3.wireOp",EDGE,"E856"),sQuery(id+"F3.wireOp",EDGE,"E857"),sQuery(id+"F3.wireOp",EDGE,"E858"),sQuery(id+"F3.wireOp",EDGE,"E859"),sQuery(id+"F3.wireOp",EDGE,"E860"),sQuery(id+"F3.wireOp",EDGE,"E861"),sQuery(id+"F3.wireOp",EDGE,"E862")])]});
            var Q37;
            Q37=makeQuery(id+"F4.opExtrude","SWEPT_BODY",BODY,{"disambiguationData":[OSD([sQuery(id+"F3.wireOp",EDGE,"E865"),sQuery(id+"F3.wireOp",EDGE,"E866"),sQuery(id+"F3.wireOp",EDGE,"E869"),sQuery(id+"F3.wireOp",EDGE,"E870")])]});
            var Q38;
            Q38=makeQuery(id+"F4.opExtrude","SWEPT_BODY",BODY,{"disambiguationData":[OSD([sQuery(id+"F3.wireOp",EDGE,"E873"),sQuery(id+"F3.wireOp",EDGE,"E875"),sQuery(id+"F3.wireOp",EDGE,"E877"),sQuery(id+"F3.wireOp",EDGE,"E878")])]});
            var Q39;
            Q39=makeQuery(id+"F4.opExtrude","SWEPT_BODY",BODY,{"disambiguationData":[OSD([sQuery(id+"F3.wireOp",EDGE,"E881"),sQuery(id+"F3.wireOp",EDGE,"E882"),sQuery(id+"F3.wireOp",EDGE,"E883"),sQuery(id+"F3.wireOp",EDGE,"E884"),sQuery(id+"F3.wireOp",EDGE,"E885"),sQuery(id+"F3.wireOp",EDGE,"E886"),sQuery(id+"F3.wireOp",EDGE,"E887"),sQuery(id+"F3.wireOp",EDGE,"E888"),sQuery(id+"F3.wireOp",EDGE,"E889"),sQuery(id+"F3.wireOp",EDGE,"E890"),sQuery(id+"F3.wireOp",EDGE,"E891"),sQuery(id+"F3.wireOp",EDGE,"E892"),sQuery(id+"F3.wireOp",EDGE,"E893"),sQuery(id+"F3.wireOp",EDGE,"E894"),sQuery(id+"F3.wireOp",EDGE,"E895"),sQuery(id+"F3.wireOp",EDGE,"E896")])]});
            var Q40;
            Q40=makeQuery(id+"F4.opExtrude","SWEPT_BODY",BODY,{"disambiguationData":[OSD([sQuery(id+"F3.wireOp",EDGE,"E899"),sQuery(id+"F3.wireOp",EDGE,"E900"),sQuery(id+"F3.wireOp",EDGE,"E903"),sQuery(id+"F3.wireOp",EDGE,"E904")])]});
            var Q41;
            Q41=makeQuery(id+"F4.opExtrude","SWEPT_BODY",BODY,{"disambiguationData":[OSD([sQuery(id+"F3.wireOp",EDGE,"E907"),sQuery(id+"F3.wireOp",EDGE,"E909"),sQuery(id+"F3.wireOp",EDGE,"E911"),sQuery(id+"F3.wireOp",EDGE,"E912")])]});
            var Q42;
            Q42=makeQuery(id+"F4.opExtrude","SWEPT_BODY",BODY,{"disambiguationData":[OSD([sQuery(id+"F3.wireOp",EDGE,"E915"),sQuery(id+"F3.wireOp",EDGE,"E916"),sQuery(id+"F3.wireOp",EDGE,"E917"),sQuery(id+"F3.wireOp",EDGE,"E918"),sQuery(id+"F3.wireOp",EDGE,"E919"),sQuery(id+"F3.wireOp",EDGE,"E920"),sQuery(id+"F3.wireOp",EDGE,"E921"),sQuery(id+"F3.wireOp",EDGE,"E922"),sQuery(id+"F3.wireOp",EDGE,"E923"),sQuery(id+"F3.wireOp",EDGE,"E924"),sQuery(id+"F3.wireOp",EDGE,"E925"),sQuery(id+"F3.wireOp",EDGE,"E926"),sQuery(id+"F3.wireOp",EDGE,"E927"),sQuery(id+"F3.wireOp",EDGE,"E928"),sQuery(id+"F3.wireOp",EDGE,"E929"),sQuery(id+"F3.wireOp",EDGE,"E930")])]});
            var Q43;
            Q43=makeQuery(id+"F4.opExtrude","SWEPT_BODY",BODY,{"disambiguationData":[OSD([sQuery(id+"F3.wireOp",EDGE,"E933"),sQuery(id+"F3.wireOp",EDGE,"E934"),sQuery(id+"F3.wireOp",EDGE,"E935"),sQuery(id+"F3.wireOp",EDGE,"E936")])]});
            var Q44;
            Q44=makeQuery(id+"F4.opExtrude","SWEPT_BODY",BODY,{"disambiguationData":[OSD([sQuery(id+"F3.wireOp",EDGE,"E941"),sQuery(id+"F3.wireOp",EDGE,"E943"),sQuery(id+"F3.wireOp",EDGE,"E945"),sQuery(id+"F3.wireOp",EDGE,"E946")])]});
            var Q45;
            Q45=makeQuery(id+"F4.opExtrude","SWEPT_BODY",BODY,{"disambiguationData":[OSD([sQuery(id+"F3.wireOp",EDGE,"E949"),sQuery(id+"F3.wireOp",EDGE,"E950"),sQuery(id+"F3.wireOp",EDGE,"E951"),sQuery(id+"F3.wireOp",EDGE,"E952"),sQuery(id+"F3.wireOp",EDGE,"E953"),sQuery(id+"F3.wireOp",EDGE,"E954"),sQuery(id+"F3.wireOp",EDGE,"E955"),sQuery(id+"F3.wireOp",EDGE,"E956"),sQuery(id+"F3.wireOp",EDGE,"E957"),sQuery(id+"F3.wireOp",EDGE,"E958"),sQuery(id+"F3.wireOp",EDGE,"E959"),sQuery(id+"F3.wireOp",EDGE,"E960"),sQuery(id+"F3.wireOp",EDGE,"E961"),sQuery(id+"F3.wireOp",EDGE,"E962"),sQuery(id+"F3.wireOp",EDGE,"E963"),sQuery(id+"F3.wireOp",EDGE,"E964")])]});
            var Q46;
            Q46=makeQuery(id+"F4.opExtrude","SWEPT_BODY",BODY,{"disambiguationData":[OSD([sQuery(id+"F3.wireOp",EDGE,"E967"),sQuery(id+"F3.wireOp",EDGE,"E968"),sQuery(id+"F3.wireOp",EDGE,"E971"),sQuery(id+"F3.wireOp",EDGE,"E972")])]});
            var Q47;
            Q47=makeQuery(id+"F4.opExtrude","SWEPT_BODY",BODY,{"disambiguationData":[OSD([sQuery(id+"F3.wireOp",EDGE,"E975"),sQuery(id+"F3.wireOp",EDGE,"E977"),sQuery(id+"F3.wireOp",EDGE,"E979"),sQuery(id+"F3.wireOp",EDGE,"E980")])]});
            var Q48;
            Q48=makeQuery(id+"F4.opExtrude","SWEPT_BODY",BODY,{"disambiguationData":[OSD([sQuery(id+"F3.wireOp",EDGE,"E398"),sQuery(id+"F3.wireOp",EDGE,"E400"),sQuery(id+"F3.wireOp",EDGE,"E401"),sQuery(id+"F3.wireOp",EDGE,"E402")])]});
            var Q49;
            Q49=makeQuery(id+"F4.opExtrude","SWEPT_BODY",BODY,{"disambiguationData":[OSD([sQuery(id+"F3.wireOp",EDGE,"E304"),sQuery(id+"F3.wireOp",EDGE,"E305"),sQuery(id+"F3.wireOp",EDGE,"E306"),sQuery(id+"F3.wireOp",EDGE,"E307"),sQuery(id+"F3.wireOp",EDGE,"E308"),sQuery(id+"F3.wireOp",EDGE,"E309"),sQuery(id+"F3.wireOp",EDGE,"E310"),sQuery(id+"F3.wireOp",EDGE,"E311"),sQuery(id+"F3.wireOp",EDGE,"E312"),sQuery(id+"F3.wireOp",EDGE,"E313"),sQuery(id+"F3.wireOp",EDGE,"E314"),sQuery(id+"F3.wireOp",EDGE,"E315"),sQuery(id+"F3.wireOp",EDGE,"E316"),sQuery(id+"F3.wireOp",EDGE,"E317"),sQuery(id+"F3.wireOp",EDGE,"E318"),sQuery(id+"F3.wireOp",EDGE,"E319")])]});
            var Q50;
            Q50=makeQuery(id+"F4.opExtrude","SWEPT_BODY",BODY,{"disambiguationData":[OSD([sQuery(id+"F3.wireOp",EDGE,"E322"),sQuery(id+"F3.wireOp",EDGE,"E323"),sQuery(id+"F3.wireOp",EDGE,"E326"),sQuery(id+"F3.wireOp",EDGE,"E327")])]});
            var Q51;
            Q51=makeQuery(id+"F4.opExtrude","SWEPT_BODY",BODY,{"disambiguationData":[OSD([sQuery(id+"F3.wireOp",EDGE,"E331"),sQuery(id+"F3.wireOp",EDGE,"E333"),sQuery(id+"F3.wireOp",EDGE,"E334"),sQuery(id+"F3.wireOp",EDGE,"E335")])]});
            var Q52;
            Q52=makeQuery(id+"F4.opExtrude","SWEPT_BODY",BODY,{"disambiguationData":[OSD([sQuery(id+"F3.wireOp",EDGE,"E338"),sQuery(id+"F3.wireOp",EDGE,"E339"),sQuery(id+"F3.wireOp",EDGE,"E340"),sQuery(id+"F3.wireOp",EDGE,"E341"),sQuery(id+"F3.wireOp",EDGE,"E342"),sQuery(id+"F3.wireOp",EDGE,"E343"),sQuery(id+"F3.wireOp",EDGE,"E344"),sQuery(id+"F3.wireOp",EDGE,"E345"),sQuery(id+"F3.wireOp",EDGE,"E346"),sQuery(id+"F3.wireOp",EDGE,"E347"),sQuery(id+"F3.wireOp",EDGE,"E348"),sQuery(id+"F3.wireOp",EDGE,"E349"),sQuery(id+"F3.wireOp",EDGE,"E350"),sQuery(id+"F3.wireOp",EDGE,"E351"),sQuery(id+"F3.wireOp",EDGE,"E352"),sQuery(id+"F3.wireOp",EDGE,"E353")])]});
            var Q53;
            Q53=makeQuery(id+"F4.opExtrude","SWEPT_BODY",BODY,{"disambiguationData":[OSD([sQuery(id+"F3.wireOp",EDGE,"E356"),sQuery(id+"F3.wireOp",EDGE,"E357"),sQuery(id+"F3.wireOp",EDGE,"E360"),sQuery(id+"F3.wireOp",EDGE,"E361")])]});
            var Q54;
            Q54=makeQuery(id+"F4.opExtrude","SWEPT_BODY",BODY,{"disambiguationData":[OSD([sQuery(id+"F3.wireOp",EDGE,"E364"),sQuery(id+"F3.wireOp",EDGE,"E366"),sQuery(id+"F3.wireOp",EDGE,"E367"),sQuery(id+"F3.wireOp",EDGE,"E368")])]});
            var Q55;
            Q55=makeQuery(id+"F4.opExtrude","SWEPT_BODY",BODY,{"disambiguationData":[OSD([sQuery(id+"F3.wireOp",EDGE,"E371"),sQuery(id+"F3.wireOp",EDGE,"E372"),sQuery(id+"F3.wireOp",EDGE,"E373"),sQuery(id+"F3.wireOp",EDGE,"E374"),sQuery(id+"F3.wireOp",EDGE,"E375"),sQuery(id+"F3.wireOp",EDGE,"E376"),sQuery(id+"F3.wireOp",EDGE,"E377"),sQuery(id+"F3.wireOp",EDGE,"E378"),sQuery(id+"F3.wireOp",EDGE,"E379"),sQuery(id+"F3.wireOp",EDGE,"E380"),sQuery(id+"F3.wireOp",EDGE,"E381"),sQuery(id+"F3.wireOp",EDGE,"E382"),sQuery(id+"F3.wireOp",EDGE,"E383"),sQuery(id+"F3.wireOp",EDGE,"E384"),sQuery(id+"F3.wireOp",EDGE,"E385"),sQuery(id+"F3.wireOp",EDGE,"E386")])]});
            var Q56;
            Q56=makeQuery(id+"F4.opExtrude","SWEPT_BODY",BODY,{"disambiguationData":[OSD([sQuery(id+"F3.wireOp",EDGE,"E389"),sQuery(id+"F3.wireOp",EDGE,"E390"),sQuery(id+"F3.wireOp",EDGE,"E393"),sQuery(id+"F3.wireOp",EDGE,"E394")])]});
            var Q57;
            Q57=makeQuery(id+"F4.opExtrude","SWEPT_BODY",BODY,{"disambiguationData":[OSD([sQuery(id+"F3.wireOp",EDGE,"E405"),sQuery(id+"F3.wireOp",EDGE,"E406"),sQuery(id+"F3.wireOp",EDGE,"E407"),sQuery(id+"F3.wireOp",EDGE,"E408"),sQuery(id+"F3.wireOp",EDGE,"E409"),sQuery(id+"F3.wireOp",EDGE,"E410"),sQuery(id+"F3.wireOp",EDGE,"E411"),sQuery(id+"F3.wireOp",EDGE,"E412"),sQuery(id+"F3.wireOp",EDGE,"E413"),sQuery(id+"F3.wireOp",EDGE,"E414"),sQuery(id+"F3.wireOp",EDGE,"E415"),sQuery(id+"F3.wireOp",EDGE,"E416"),sQuery(id+"F3.wireOp",EDGE,"E417"),sQuery(id+"F3.wireOp",EDGE,"E418"),sQuery(id+"F3.wireOp",EDGE,"E419"),sQuery(id+"F3.wireOp",EDGE,"E420")])]});
            var Q58;
            Q58=makeQuery(id+"F4.opExtrude","SWEPT_BODY",BODY,{"disambiguationData":[OSD([sQuery(id+"F3.wireOp",EDGE,"E609"),sQuery(id+"F3.wireOp",EDGE,"E610"),sQuery(id+"F3.wireOp",EDGE,"E611"),sQuery(id+"F3.wireOp",EDGE,"E612"),sQuery(id+"F3.wireOp",EDGE,"E613"),sQuery(id+"F3.wireOp",EDGE,"E614"),sQuery(id+"F3.wireOp",EDGE,"E615"),sQuery(id+"F3.wireOp",EDGE,"E616"),sQuery(id+"F3.wireOp",EDGE,"E617"),sQuery(id+"F3.wireOp",EDGE,"E618"),sQuery(id+"F3.wireOp",EDGE,"E619"),sQuery(id+"F3.wireOp",EDGE,"E620"),sQuery(id+"F3.wireOp",EDGE,"E621"),sQuery(id+"F3.wireOp",EDGE,"E622"),sQuery(id+"F3.wireOp",EDGE,"E623"),sQuery(id+"F3.wireOp",EDGE,"E624")])]});
            deleteBodies(context, id + "F5", {"entities" : qUnion([Q0, Q1, Q2, Q3, Q4, Q5, Q6, Q7, Q8, Q9, Q10, Q11, Q12, Q13, Q14, Q15, Q16, Q17, Q18, Q19, Q20, Q21, Q22, Q23, Q24, Q25, Q26, Q27, Q28, Q29, Q30, Q31, Q32, Q33, Q34, Q35, Q36, Q37, Q38, Q39, Q40, Q41, Q42, Q43, Q44, Q45, Q46, Q47, Q48, Q49, Q50, Q51, Q52, Q53, Q54, Q55, Q56, Q57, Q58])});
        }
    });
